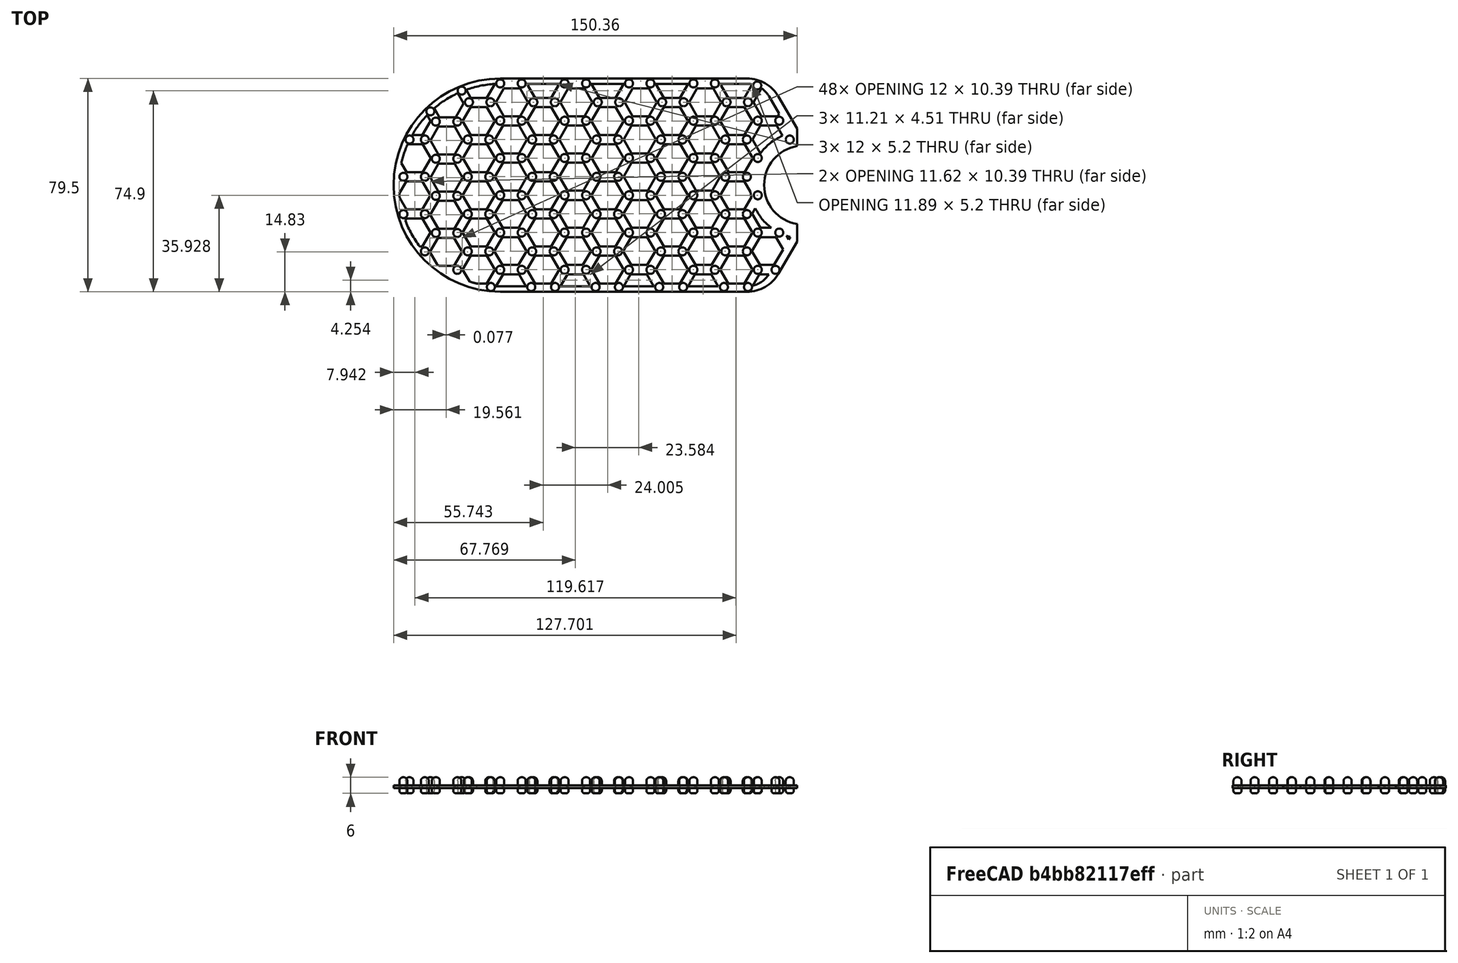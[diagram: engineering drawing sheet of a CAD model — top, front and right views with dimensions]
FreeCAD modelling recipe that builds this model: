
FCSTD DOCUMENT  (FreeCAD 1.0R39319 (Git))
Label: Soap_dryer
License: All rights reserved
LicenseURL: https://en.wikipedia.org/wiki/All_rights_reserved
objects: Sketcher::SketchObject×2, PartDesign::Pad×2, PartDesign::Fillet×2, PartDesign::Body×1
note: 17 computed .brp shape members not serialized (recipe doc carries the construction recipe); baked Part::Feature solids carry a one-line shape summary decoded from their .brp

FEATURE [Sketcher::SketchObject] Sketch
  ArcFitTolerance = 1e-06
  FullyConstrained = true
  MakeInternals = false
  sketch-geometry (463):
    g0: GeomPoint [constr] X=-7.3e-15 Y=0 Z=0
    g1: ArcOfCircle CenterX=-7.3e-15 CenterY=0 CenterZ=0 NormalX=0 NormalY=0 NormalZ=1 AngleXU=0 Radius=39.75 StartAngle=1.5708 EndAngle=4.71239
    g2: GeomPoint [constr] X=113.11 Y=0 Z=0
    g3: GeomPoint [constr] X=110.61 Y=14.5366 Z=0
    g4: GeomPoint [constr] X=110.61 Y=-14.5366 Z=0
    g5: ArcOfCircle CenterX=113.11 CenterY=0 CenterZ=0 NormalX=0 NormalY=0 NormalZ=1 AngleXU=0 Radius=14.75 StartAngle=1.74111 EndAngle=4.54208
    g6: LineSegment StartX=-7.3e-15 StartY=39.75 StartZ=0 EndX=92 EndY=39.75 EndZ=0
    g7: LineSegment StartX=-7.3e-15 StartY=-39.75 StartZ=0 EndX=92 EndY=-39.75 EndZ=0
    g8: GeomPoint [constr] X=98.11 Y=39.75 Z=0
    g9: ArcOfCircle CenterX=92 CenterY=-26.25 CenterZ=0 NormalX=0 NormalY=0 NormalZ=1 AngleXU=0 Radius=13.5 StartAngle=4.71239 EndAngle=5.75886
    g10: GeomPoint [constr] X=98.11 Y=-39.75 Z=0
    g11: ArcOfCircle [constr] CenterX=-7.3e-15 CenterY=0 CenterZ=0 NormalX=0 NormalY=0 NormalZ=1 AngleXU=0 Radius=37.75 StartAngle=1.5708 EndAngle=4.71239
    g12: LineSegment [constr] StartX=0 StartY=37.75 StartZ=0 EndX=92 EndY=37.75 EndZ=0
    g13: LineSegment [constr] StartX=100.219 StartY=33.0085 StartZ=0 EndX=108.11 EndY=19.3649 EndZ=0
    g14: ArcOfCircle [constr] CenterX=113.11 CenterY=0 CenterZ=0 NormalX=0 NormalY=0 NormalZ=1 AngleXU=0 Radius=20 StartAngle=1.82349 EndAngle=4.4597
    g15: ArcOfCircle [constr] CenterX=92 CenterY=28.255 CenterZ=0 NormalX=0 NormalY=0 NormalZ=1 AngleXU=0 Radius=9.49497 StartAngle=0.524324 EndAngle=1.5708
    g16: GeomPoint [constr] X=97.4773 Y=37.75 Z=0
    g17: LineSegment [constr] StartX=0 StartY=-37.75 StartZ=0 EndX=92 EndY=-37.75 EndZ=0
    g18: LineSegment [constr] StartX=100.219 StartY=-33.0085 StartZ=0 EndX=108.11 EndY=-19.3649 EndZ=0
    g19: ArcOfCircle [constr] CenterX=92 CenterY=-28.255 CenterZ=0 NormalX=0 NormalY=0 NormalZ=1 AngleXU=0 Radius=9.49497 StartAngle=4.71239 EndAngle=5.75886
    g20: GeomPoint [constr] X=97.4773 Y=-37.75 Z=0
    g21: LineSegment [constr] StartX=92 StartY=-39.75 StartZ=0 EndX=92 EndY=-37.75 EndZ=0
    g22: LineSegment StartX=110.61 StartY=14.5366 StartZ=0 EndX=110.61 EndY=21.0366 EndZ=0
    g23: LineSegment StartX=110.61 StartY=21.0366 StartZ=0 EndX=103.686 EndY=33.0085 EndZ=0
    g24: ArcOfCircle CenterX=92 CenterY=26.25 CenterZ=0 NormalX=0 NormalY=0 NormalZ=1 AngleXU=0 Radius=13.5 StartAngle=0.524324 EndAngle=1.5708
    g25: LineSegment StartX=110.61 StartY=-14.5366 StartZ=0 EndX=110.61 EndY=-21.0366 EndZ=0
    g26: LineSegment StartX=103.686 StartY=-33.0085 StartZ=0 EndX=110.61 EndY=-21.0366 EndZ=0
    g27: LineSegment StartX=10.3593 StartY=30.8238 StartZ=0 EndX=7.35933 EndY=36.02 EndZ=0
    g28: LineSegment StartX=7.35933 StartY=36.02 StartZ=0 EndX=1.35933 EndY=36.02 EndZ=0
    g29: LineSegment StartX=1.35933 StartY=36.02 StartZ=0 EndX=-1.64067 EndY=30.8238 EndZ=0
    g30: LineSegment StartX=-1.64067 StartY=30.8238 StartZ=0 EndX=1.35933 EndY=25.6277 EndZ=0
    g31: LineSegment StartX=1.35933 StartY=25.6277 StartZ=0 EndX=7.35933 EndY=25.6277 EndZ=0
    g32: LineSegment StartX=7.35933 StartY=25.6277 StartZ=0 EndX=10.3593 EndY=30.8238 EndZ=0
    g33: Circle [constr] CenterX=4.35933 CenterY=30.8238 CenterZ=0 NormalX=0 NormalY=0 NormalZ=1 AngleXU=0 Radius=6
    g34: LineSegment StartX=12.9933 StartY=32.55 StartZ=0 EndX=18.9933 EndY=32.55 EndZ=0
    g35: LineSegment StartX=12.9933 StartY=32.55 StartZ=0 EndX=9.99111 EndY=37.75 EndZ=0
    g36: LineSegment StartX=18.9933 StartY=32.55 StartZ=0 EndX=21.9956 EndY=37.75 EndZ=0
    g37: LineSegment StartX=36.9978 StartY=32.55 StartZ=0 EndX=42.9978 EndY=32.55 EndZ=0
    g38: LineSegment StartX=36.9978 StartY=32.55 StartZ=0 EndX=33.9956 EndY=37.75 EndZ=0
    g39: LineSegment StartX=42.9978 StartY=32.55 StartZ=0 EndX=46 EndY=37.75 EndZ=0
    g40: LineSegment StartX=61.0022 StartY=32.55 StartZ=0 EndX=67.0022 EndY=32.55 EndZ=0
    g41: LineSegment StartX=61.0022 StartY=32.55 StartZ=0 EndX=58 EndY=37.75 EndZ=0
    g42: LineSegment StartX=67.0022 StartY=32.55 StartZ=0 EndX=70.0044 EndY=37.75 EndZ=0
    g43: LineSegment StartX=85.0067 StartY=32.55 StartZ=0 EndX=91.0067 EndY=32.55 EndZ=0
    g44: LineSegment StartX=85.0067 StartY=32.55 StartZ=0 EndX=82.0044 EndY=37.75 EndZ=0
    g45: LineSegment StartX=91.0067 StartY=32.55 StartZ=0 EndX=93.8982 EndY=37.5583 EndZ=0
    g46: LineSegment StartX=94.3593 StartY=30.8967 StartZ=0 EndX=97.3593 EndY=25.7006 EndZ=0
    g47: LineSegment StartX=97.3593 StartY=25.7006 StartZ=0 EndX=103.359 EndY=25.7006 EndZ=0
    g48: LineSegment StartX=94.3593 StartY=30.8967 StartZ=0 EndX=97.3593 EndY=36.0929 EndZ=0
    g49: LineSegment StartX=103.359 StartY=25.7006 StartZ=0 EndX=103.902 EndY=26.6406 EndZ=0
    g50: LineSegment StartX=-22.6407 StartY=25.293 StartZ=0 EndX=-16.6407 EndY=25.293 EndZ=0
    g51: LineSegment StartX=-16.6407 StartY=25.293 StartZ=0 EndX=-13.6407 EndY=30.4891 EndZ=0
    g52: LineSegment StartX=-13.6407 StartY=30.4891 StartZ=0 EndX=-15.8252 EndY=34.2728 EndZ=0
    g53: LineSegment StartX=-26 StartY=23.883 StartZ=0 EndX=-29 EndY=18.6868 EndZ=0
    g54: LineSegment StartX=-29 StartY=18.6868 StartZ=0 EndX=-32.8004 EndY=18.6868 EndZ=0
    g55: LineSegment StartX=-26 StartY=23.883 StartZ=0 EndX=-27.2776 EndY=26.0959 EndZ=0
    g56: LineSegment StartX=-34.9123 StartY=4.83453 StartZ=0 EndX=-28.9123 EndY=4.83453 EndZ=0
    g57: LineSegment StartX=-28.9123 StartY=4.83453 StartZ=0 EndX=-25.9123 EndY=10.0307 EndZ=0
    g58: LineSegment StartX=-25.9123 StartY=10.0307 StartZ=0 EndX=-28.9123 EndY=15.2268 EndZ=0
    g59: LineSegment StartX=-28.9123 StartY=15.2268 StartZ=0 EndX=-34.5428 EndY=15.2268 EndZ=0
    g60: LineSegment StartX=-34.9123 StartY=4.83453 StartZ=0 EndX=-36.8505 EndY=8.19164 EndZ=0
    g61: LineSegment StartX=-34.9978 StartY=1.37453 StartZ=0 EndX=-28.9978 EndY=1.37453 EndZ=0
    g62: LineSegment StartX=-28.9978 StartY=1.37453 StartZ=0 EndX=-25.9978 EndY=-3.82162 EndZ=0
    g63: LineSegment StartX=-25.9978 StartY=-3.82162 StartZ=0 EndX=-28.9978 EndY=-9.01778 EndZ=0
    g64: LineSegment StartX=-28.9978 StartY=-9.01778 StartZ=0 EndX=-34.9978 EndY=-9.01778 EndZ=0
    g65: LineSegment StartX=-34.9978 StartY=-9.01778 StartZ=0 EndX=-37.4466 EndY=-4.77619 EndZ=0
    g66: LineSegment StartX=-34.9978 StartY=1.37453 StartZ=0 EndX=-37.6173 EndY=-3.16263 EndZ=0
    g67: LineSegment StartX=-35.0184 StartY=-12.4778 StartZ=0 EndX=-29.0184 EndY=-12.4778 EndZ=0
    g68: LineSegment StartX=-29.0184 StartY=-12.4778 StartZ=0 EndX=-26.0184 EndY=-17.6739 EndZ=0
    g69: LineSegment StartX=-26.0184 StartY=-17.6739 StartZ=0 EndX=-29.0184 EndY=-22.8701 EndZ=0
    g70: LineSegment StartX=-29.0184 StartY=-22.8701 StartZ=0 EndX=-30.0337 EndY=-22.8701 EndZ=0
    g71: LineSegment StartX=-35.0184 StartY=-12.4778 StartZ=0 EndX=-35.3938 EndY=-13.1279 EndZ=0
    g72: LineSegment StartX=-23.1895 StartY=-19.7239 StartZ=0 EndX=-17.1895 EndY=-19.7239 EndZ=0
    g73: LineSegment StartX=-17.1895 StartY=-19.7239 StartZ=0 EndX=-14.1895 EndY=-24.9201 EndZ=0
    g74: LineSegment StartX=-14.1895 StartY=-24.9201 StartZ=0 EndX=-17.1895 EndY=-30.1162 EndZ=0
    g75: LineSegment StartX=-23.1895 StartY=-19.7239 StartZ=0 EndX=-26.1895 EndY=-24.9201 EndZ=0
    g76: LineSegment StartX=-11 StartY=-26.3338 StartZ=0 EndX=-5.00001 EndY=-26.3338 EndZ=0
    g77: LineSegment StartX=-11 StartY=-26.3338 StartZ=0 EndX=-14 EndY=-31.5299 EndZ=0
    g78: LineSegment StartX=-14 StartY=-31.5299 StartZ=0 EndX=-11.4323 EndY=-35.9773 EndZ=0
    g79: LineSegment StartX=-5.00001 StartY=-26.3338 StartZ=0 EndX=-2.00001 EndY=-31.5299 EndZ=0
    g80: LineSegment StartX=-2.00001 StartY=-31.5299 StartZ=0 EndX=-5.00001 EndY=-36.7261 EndZ=0
    g81: LineSegment StartX=-5.00001 StartY=-36.7261 StartZ=0 EndX=-8.73249 EndY=-36.7261 EndZ=0
    g82: LineSegment StartX=57.9973 StartY=16.9715 StartZ=0 EndX=54.9973 EndY=22.1677 EndZ=0
    g83: LineSegment StartX=54.9973 StartY=22.1677 StartZ=0 EndX=48.9973 EndY=22.1677 EndZ=0
    g84: LineSegment StartX=48.9973 StartY=22.1677 StartZ=0 EndX=45.9973 EndY=16.9715 EndZ=0
    g85: LineSegment StartX=45.9973 StartY=16.9715 StartZ=0 EndX=48.9973 EndY=11.7754 EndZ=0
    g86: LineSegment StartX=48.9973 StartY=11.7754 StartZ=0 EndX=54.9973 EndY=11.7754 EndZ=0
    g87: LineSegment StartX=54.9973 StartY=11.7754 StartZ=0 EndX=57.9973 EndY=16.9715 EndZ=0
    g88: Circle [constr] CenterX=51.9973 CenterY=16.9715 CenterZ=0 NormalX=0 NormalY=0 NormalZ=1 AngleXU=0 Radius=6
    g89: LineSegment StartX=46 StartY=23.8938 StartZ=0 EndX=43 EndY=29.09 EndZ=0
    g90: LineSegment StartX=43 StartY=29.09 StartZ=0 EndX=37 EndY=29.09 EndZ=0
    g91: LineSegment StartX=37 StartY=29.09 StartZ=0 EndX=34 EndY=23.8938 EndZ=0
    g92: LineSegment StartX=34 StartY=23.8938 StartZ=0 EndX=37 EndY=18.6977 EndZ=0
    g93: LineSegment StartX=37 StartY=18.6977 StartZ=0 EndX=43 EndY=18.6977 EndZ=0
    g94: LineSegment StartX=43 StartY=18.6977 StartZ=0 EndX=46 EndY=23.8938 EndZ=0
    g95: Circle [constr] CenterX=40 CenterY=23.8938 CenterZ=0 NormalX=0 NormalY=0 NormalZ=1 AngleXU=0 Radius=6
    g96: LineSegment StartX=70 StartY=23.8938 StartZ=0 EndX=67 EndY=29.09 EndZ=0
    g97: LineSegment StartX=67 StartY=29.09 StartZ=0 EndX=61 EndY=29.09 EndZ=0
    g98: LineSegment StartX=61 StartY=29.09 StartZ=0 EndX=58 EndY=23.8938 EndZ=0
    g99: LineSegment StartX=58 StartY=23.8938 StartZ=0 EndX=61 EndY=18.6977 EndZ=0
    g100: LineSegment StartX=61 StartY=18.6977 StartZ=0 EndX=67 EndY=18.6977 EndZ=0
    g101: LineSegment StartX=67 StartY=18.6977 StartZ=0 EndX=70 EndY=23.8938 EndZ=0
    g102: Circle [constr] CenterX=64 CenterY=23.8938 CenterZ=0 NormalX=0 NormalY=0 NormalZ=1 AngleXU=0 Radius=6
    g103: LineSegment StartX=82.3593 StartY=30.8238 StartZ=0 EndX=79.3593 EndY=36.02 EndZ=0
    g104: LineSegment StartX=79.3593 StartY=36.02 StartZ=0 EndX=73.3593 EndY=36.02 EndZ=0
    g105: LineSegment StartX=73.3593 StartY=36.02 StartZ=0 EndX=70.3593 EndY=30.8238 EndZ=0
    g106: LineSegment StartX=70.3593 StartY=30.8238 StartZ=0 EndX=73.3593 EndY=25.6277 EndZ=0
    g107: LineSegment StartX=73.3593 StartY=25.6277 StartZ=0 EndX=79.3593 EndY=25.6277 EndZ=0
    g108: LineSegment StartX=79.3593 StartY=25.6277 StartZ=0 EndX=82.3593 EndY=30.8238 EndZ=0
    g109: Circle [constr] CenterX=76.3593 CenterY=30.8238 CenterZ=0 NormalX=0 NormalY=0 NormalZ=1 AngleXU=0 Radius=6
    g110: LineSegment StartX=94 StartY=23.8938 StartZ=0 EndX=91 EndY=29.09 EndZ=0
    g111: LineSegment StartX=91 StartY=29.09 StartZ=0 EndX=85 EndY=29.09 EndZ=0
    g112: LineSegment StartX=85 StartY=29.09 StartZ=0 EndX=82 EndY=23.8938 EndZ=0
    g113: LineSegment StartX=82 StartY=23.8938 StartZ=0 EndX=85 EndY=18.6977 EndZ=0
    g114: LineSegment StartX=85 StartY=18.6977 StartZ=0 EndX=91 EndY=18.6977 EndZ=0
    g115: LineSegment StartX=91 StartY=18.6977 StartZ=0 EndX=94 EndY=23.8938 EndZ=0
    g116: Circle [constr] CenterX=88 CenterY=23.8938 CenterZ=0 NormalX=0 NormalY=0 NormalZ=1 AngleXU=0 Radius=6
    g117: LineSegment StartX=58.3593 StartY=30.8238 StartZ=0 EndX=55.3593 EndY=36.02 EndZ=0
    g118: LineSegment StartX=55.3593 StartY=36.02 StartZ=0 EndX=49.3593 EndY=36.02 EndZ=0
    g119: LineSegment StartX=49.3593 StartY=36.02 StartZ=0 EndX=46.3593 EndY=30.8238 EndZ=0
    g120: LineSegment StartX=46.3593 StartY=30.8238 StartZ=0 EndX=49.3593 EndY=25.6277 EndZ=0
    g121: LineSegment StartX=49.3593 StartY=25.6277 StartZ=0 EndX=55.3593 EndY=25.6277 EndZ=0
    g122: LineSegment StartX=55.3593 StartY=25.6277 StartZ=0 EndX=58.3593 EndY=30.8238 EndZ=0
    g123: Circle [constr] CenterX=52.3593 CenterY=30.8238 CenterZ=0 NormalX=0 NormalY=0 NormalZ=1 AngleXU=0 Radius=6
    g124: LineSegment StartX=34.3593 StartY=30.8238 StartZ=0 EndX=31.3593 EndY=36.02 EndZ=0
    g125: LineSegment StartX=31.3593 StartY=36.02 StartZ=0 EndX=25.3593 EndY=36.02 EndZ=0
    g126: LineSegment StartX=25.3593 StartY=36.02 StartZ=0 EndX=22.3593 EndY=30.8238 EndZ=0
    g127: LineSegment StartX=22.3593 StartY=30.8238 StartZ=0 EndX=25.3593 EndY=25.6277 EndZ=0
    g128: LineSegment StartX=25.3593 StartY=25.6277 StartZ=0 EndX=31.3593 EndY=25.6277 EndZ=0
    g129: LineSegment StartX=31.3593 StartY=25.6277 StartZ=0 EndX=34.3593 EndY=30.8238 EndZ=0
    g130: Circle [constr] CenterX=28.3593 CenterY=30.8238 CenterZ=0 NormalX=0 NormalY=0 NormalZ=1 AngleXU=0 Radius=6
    g131: LineSegment StartX=22 StartY=23.8938 StartZ=0 EndX=19 EndY=29.09 EndZ=0
    g132: LineSegment StartX=19 StartY=29.09 StartZ=0 EndX=13 EndY=29.09 EndZ=0
    g133: LineSegment StartX=13 StartY=29.09 StartZ=0 EndX=10 EndY=23.8938 EndZ=0
    g134: LineSegment StartX=10 StartY=23.8938 StartZ=0 EndX=13 EndY=18.6977 EndZ=0
    g135: LineSegment StartX=13 StartY=18.6977 StartZ=0 EndX=19 EndY=18.6977 EndZ=0
    g136: LineSegment StartX=19 StartY=18.6977 StartZ=0 EndX=22 EndY=23.8938 EndZ=0
    g137: Circle [constr] CenterX=16 CenterY=23.8938 CenterZ=0 NormalX=0 NormalY=0 NormalZ=1 AngleXU=0 Radius=6
    g138: LineSegment StartX=9.99732 StartY=16.9715 StartZ=0 EndX=6.99732 EndY=22.1677 EndZ=0
    g139: LineSegment StartX=6.99732 StartY=22.1677 StartZ=0 EndX=0.997325 EndY=22.1677 EndZ=0
    g140: LineSegment StartX=0.997325 StartY=22.1677 StartZ=0 EndX=-2.00268 EndY=16.9715 EndZ=0
    g141: LineSegment StartX=-2.00268 StartY=16.9715 StartZ=0 EndX=0.997325 EndY=11.7754 EndZ=0
    g142: LineSegment StartX=0.997325 StartY=11.7754 StartZ=0 EndX=6.99732 EndY=11.7754 EndZ=0
    g143: LineSegment StartX=6.99732 StartY=11.7754 StartZ=0 EndX=9.99732 EndY=16.9715 EndZ=0
    g144: Circle [constr] CenterX=3.99732 CenterY=16.9715 CenterZ=0 NormalX=0 NormalY=0 NormalZ=1 AngleXU=0 Radius=6
    g145: LineSegment StartX=-2 StartY=23.8793 StartZ=0 EndX=-5 EndY=29.0754 EndZ=0
    g146: LineSegment StartX=-5 StartY=29.0754 StartZ=0 EndX=-11 EndY=29.0754 EndZ=0
    g147: LineSegment StartX=-11 StartY=29.0754 StartZ=0 EndX=-14 EndY=23.8793 EndZ=0
    g148: LineSegment StartX=-14 StartY=23.8793 StartZ=0 EndX=-11 EndY=18.6831 EndZ=0
    g149: LineSegment StartX=-11 StartY=18.6831 StartZ=0 EndX=-5 EndY=18.6831 EndZ=0
    g150: LineSegment StartX=-5 StartY=18.6831 StartZ=0 EndX=-2 EndY=23.8793 EndZ=0
    g151: Circle [constr] CenterX=-8 CenterY=23.8793 CenterZ=0 NormalX=0 NormalY=0 NormalZ=1 AngleXU=0 Radius=6
    g152: LineSegment StartX=-14.0027 StartY=16.6368 StartZ=0 EndX=-17.0027 EndY=21.833 EndZ=0
    g153: LineSegment StartX=-17.0027 StartY=21.833 StartZ=0 EndX=-23.0027 EndY=21.833 EndZ=0
    g154: LineSegment StartX=-23.0027 StartY=21.833 StartZ=0 EndX=-26.0027 EndY=16.6368 EndZ=0
    g155: LineSegment StartX=-26.0027 StartY=16.6368 StartZ=0 EndX=-23.0027 EndY=11.4407 EndZ=0
    g156: LineSegment StartX=-23.0027 StartY=11.4407 StartZ=0 EndX=-17.0027 EndY=11.4407 EndZ=0
    g157: LineSegment StartX=-17.0027 StartY=11.4407 StartZ=0 EndX=-14.0027 EndY=16.6368 EndZ=0
    g158: Circle [constr] CenterX=-20.0027 CenterY=16.6368 CenterZ=0 NormalX=0 NormalY=0 NormalZ=1 AngleXU=0 Radius=6
    g159: LineSegment StartX=-1.91227 StartY=10.027 StartZ=0 EndX=-4.91227 EndY=15.2231 EndZ=0
    g160: LineSegment StartX=-4.91227 StartY=15.2231 StartZ=0 EndX=-10.9123 EndY=15.2231 EndZ=0
    g161: LineSegment StartX=-10.9123 StartY=15.2231 StartZ=0 EndX=-13.9123 EndY=10.027 EndZ=0
    g162: LineSegment StartX=-13.9123 StartY=10.027 StartZ=0 EndX=-10.9123 EndY=4.83082 EndZ=0
    g163: LineSegment StartX=-10.9123 StartY=4.83082 StartZ=0 EndX=-4.91227 EndY=4.83082 EndZ=0
    g164: LineSegment StartX=-4.91227 StartY=4.83082 StartZ=0 EndX=-1.91227 EndY=10.027 EndZ=0
    g165: Circle [constr] CenterX=-7.91227 CenterY=10.027 CenterZ=0 NormalX=0 NormalY=0 NormalZ=1 AngleXU=0 Radius=6
    g166: LineSegment StartX=-14 StartY=2.78453 StartZ=0 EndX=-17 EndY=7.98068 EndZ=0
    g167: LineSegment StartX=-17 StartY=7.98068 StartZ=0 EndX=-23 EndY=7.98068 EndZ=0
    g168: LineSegment StartX=-23 StartY=7.98068 StartZ=0 EndX=-26 EndY=2.78453 EndZ=0
    g169: LineSegment StartX=-26 StartY=2.78453 StartZ=0 EndX=-23 EndY=-2.41162 EndZ=0
    g170: LineSegment StartX=-23 StartY=-2.41162 StartZ=0 EndX=-17 EndY=-2.41162 EndZ=0
    g171: LineSegment StartX=-17 StartY=-2.41162 StartZ=0 EndX=-14 EndY=2.78453 EndZ=0
    g172: Circle [constr] CenterX=-20 CenterY=2.78453 CenterZ=0 NormalX=0 NormalY=0 NormalZ=1 AngleXU=0 Radius=6
    g173: LineSegment StartX=-14.1129 StartY=-11.0678 StartZ=0 EndX=-17.1129 EndY=-5.87162 EndZ=0
    g174: LineSegment StartX=-17.1129 StartY=-5.87162 StartZ=0 EndX=-23.1129 EndY=-5.87162 EndZ=0
    g175: LineSegment StartX=-23.1129 StartY=-5.87162 StartZ=0 EndX=-26.1129 EndY=-11.0678 EndZ=0
    g176: LineSegment StartX=-26.1129 StartY=-11.0678 StartZ=0 EndX=-23.1129 EndY=-16.2639 EndZ=0
    g177: LineSegment StartX=-23.1129 StartY=-16.2639 StartZ=0 EndX=-17.1129 EndY=-16.2639 EndZ=0
    g178: LineSegment StartX=-17.1129 StartY=-16.2639 StartZ=0 EndX=-14.1129 EndY=-11.0678 EndZ=0
    g179: Circle [constr] CenterX=-20.1129 CenterY=-11.0678 CenterZ=0 NormalX=0 NormalY=0 NormalZ=1 AngleXU=0 Radius=6
    g180: LineSegment StartX=-1.99776 StartY=-3.82533 StartZ=0 EndX=-4.99776 EndY=1.37082 EndZ=0
    g181: LineSegment StartX=-4.99776 StartY=1.37082 StartZ=0 EndX=-10.9978 EndY=1.37082 EndZ=0
    g182: LineSegment StartX=-10.9978 StartY=1.37082 StartZ=0 EndX=-13.9978 EndY=-3.82533 EndZ=0
    g183: LineSegment StartX=-13.9978 StartY=-3.82533 StartZ=0 EndX=-10.9978 EndY=-9.02149 EndZ=0
    g184: LineSegment StartX=-10.9978 StartY=-9.02149 StartZ=0 EndX=-4.99776 EndY=-9.02149 EndZ=0
    g185: LineSegment StartX=-4.99776 StartY=-9.02149 StartZ=0 EndX=-1.99776 EndY=-3.82533 EndZ=0
    g186: Circle [constr] CenterX=-7.99776 CenterY=-3.82533 CenterZ=0 NormalX=0 NormalY=0 NormalZ=1 AngleXU=0 Radius=6
    g187: LineSegment StartX=-2.0184 StartY=-17.6776 StartZ=0 EndX=-5.0184 EndY=-12.4815 EndZ=0
    g188: LineSegment StartX=-5.0184 StartY=-12.4815 StartZ=0 EndX=-11.0184 EndY=-12.4815 EndZ=0
    g189: LineSegment StartX=-11.0184 StartY=-12.4815 StartZ=0 EndX=-14.0184 EndY=-17.6776 EndZ=0
    g190: LineSegment StartX=-14.0184 StartY=-17.6776 StartZ=0 EndX=-11.0184 EndY=-22.8738 EndZ=0
    g191: LineSegment StartX=-11.0184 StartY=-22.8738 StartZ=0 EndX=-5.0184 EndY=-22.8738 EndZ=0
    g192: LineSegment StartX=-5.0184 StartY=-22.8738 StartZ=0 EndX=-2.0184 EndY=-17.6776 EndZ=0
    g193: Circle [constr] CenterX=-8.0184 CenterY=-17.6776 CenterZ=0 NormalX=0 NormalY=0 NormalZ=1 AngleXU=0 Radius=6
    g194: LineSegment StartX=9.81053 StartY=-24.5854 StartZ=0 EndX=6.81053 EndY=-19.3892 EndZ=0
    g195: LineSegment StartX=6.81053 StartY=-19.3892 StartZ=0 EndX=0.81053 EndY=-19.3892 EndZ=0
    g196: LineSegment StartX=0.81053 StartY=-19.3892 StartZ=0 EndX=-2.18947 EndY=-24.5854 EndZ=0
    g197: LineSegment StartX=-2.18947 StartY=-24.5854 StartZ=0 EndX=0.81053 EndY=-29.7815 EndZ=0
    g198: LineSegment StartX=0.81053 StartY=-29.7815 StartZ=0 EndX=6.81053 EndY=-29.7815 EndZ=0
    g199: LineSegment StartX=6.81053 StartY=-29.7815 StartZ=0 EndX=9.81053 EndY=-24.5854 EndZ=0
    g200: Circle [constr] CenterX=3.81053 CenterY=-24.5854 CenterZ=0 NormalX=0 NormalY=0 NormalZ=1 AngleXU=0 Radius=6
    g201: LineSegment StartX=7.01885 StartY=-33.2415 StartZ=0 EndX=1.01885 EndY=-33.2415 EndZ=0
    g202: LineSegment StartX=1.01885 StartY=-33.2415 StartZ=0 EndX=-1.56537 EndY=-37.7175 EndZ=0
    g203: LineSegment StartX=7.01885 StartY=-33.2415 StartZ=0 EndX=9.62182 EndY=-37.75 EndZ=0
    g204: LineSegment StartX=10 StartY=3.11924 StartZ=0 EndX=7 EndY=8.31539 EndZ=0
    g205: LineSegment StartX=7 StartY=8.31539 StartZ=0 EndX=1 EndY=8.31539 EndZ=0
    g206: LineSegment StartX=1 StartY=8.31539 StartZ=0 EndX=-2 EndY=3.11924 EndZ=0
    g207: LineSegment StartX=-2 StartY=3.11924 StartZ=0 EndX=1 EndY=-2.07691 EndZ=0
    g208: LineSegment StartX=1 StartY=-2.07691 StartZ=0 EndX=7 EndY=-2.07691 EndZ=0
    g209: LineSegment StartX=7 StartY=-2.07691 StartZ=0 EndX=10 EndY=3.11924 EndZ=0
    g210: Circle [constr] CenterX=4 CenterY=3.11924 CenterZ=0 NormalX=0 NormalY=0 NormalZ=1 AngleXU=0 Radius=6
    g211: LineSegment StartX=22.0877 StartY=10.0415 StartZ=0 EndX=19.0877 EndY=15.2377 EndZ=0
    g212: LineSegment StartX=19.0877 StartY=15.2377 StartZ=0 EndX=13.0877 EndY=15.2377 EndZ=0
    g213: LineSegment StartX=13.0877 StartY=15.2377 StartZ=0 EndX=10.0877 EndY=10.0415 EndZ=0
    g214: LineSegment StartX=10.0877 StartY=10.0415 StartZ=0 EndX=13.0877 EndY=4.84539 EndZ=0
    g215: LineSegment StartX=13.0877 StartY=4.84539 StartZ=0 EndX=19.0877 EndY=4.84539 EndZ=0
    g216: LineSegment StartX=19.0877 StartY=4.84539 StartZ=0 EndX=22.0877 EndY=10.0415 EndZ=0
    g217: Circle [constr] CenterX=16.0877 CenterY=10.0415 CenterZ=0 NormalX=0 NormalY=0 NormalZ=1 AngleXU=0 Radius=6
    g218: LineSegment StartX=33.9973 StartY=16.9715 StartZ=0 EndX=30.9973 EndY=22.1677 EndZ=0
    g219: LineSegment StartX=30.9973 StartY=22.1677 StartZ=0 EndX=24.9973 EndY=22.1677 EndZ=0
    g220: LineSegment StartX=24.9973 StartY=22.1677 StartZ=0 EndX=21.9973 EndY=16.9715 EndZ=0
    g221: LineSegment StartX=21.9973 StartY=16.9715 StartZ=0 EndX=24.9973 EndY=11.7754 EndZ=0
    g222: LineSegment StartX=24.9973 StartY=11.7754 StartZ=0 EndX=30.9973 EndY=11.7754 EndZ=0
    g223: LineSegment StartX=30.9973 StartY=11.7754 StartZ=0 EndX=33.9973 EndY=16.9715 EndZ=0
    g224: Circle [constr] CenterX=27.9973 CenterY=16.9715 CenterZ=0 NormalX=0 NormalY=0 NormalZ=1 AngleXU=0 Radius=6
    g225: LineSegment StartX=9.88715 StartY=-10.7331 StartZ=0 EndX=6.88715 EndY=-5.53691 EndZ=0
    g226: LineSegment StartX=6.88715 StartY=-5.53691 StartZ=0 EndX=0.887149 EndY=-5.53691 EndZ=0
    g227: LineSegment StartX=0.887149 StartY=-5.53691 StartZ=0 EndX=-2.11285 EndY=-10.7331 EndZ=0
    g228: LineSegment StartX=-2.11285 StartY=-10.7331 StartZ=0 EndX=0.887149 EndY=-15.9292 EndZ=0
    g229: LineSegment StartX=0.887149 StartY=-15.9292 StartZ=0 EndX=6.88715 EndY=-15.9292 EndZ=0
    g230: LineSegment StartX=6.88715 StartY=-15.9292 StartZ=0 EndX=9.88715 EndY=-10.7331 EndZ=0
    g231: Circle [constr] CenterX=3.88715 CenterY=-10.7331 CenterZ=0 NormalX=0 NormalY=0 NormalZ=1 AngleXU=0 Radius=6
    g232: LineSegment StartX=22.0022 StartY=-3.81076 StartZ=0 EndX=19.0022 EndY=1.38539 EndZ=0
    g233: LineSegment StartX=19.0022 StartY=1.38539 StartZ=0 EndX=13.0022 EndY=1.38539 EndZ=0
    g234: LineSegment StartX=13.0022 StartY=1.38539 StartZ=0 EndX=10.0022 EndY=-3.81076 EndZ=0
    g235: LineSegment StartX=10.0022 StartY=-3.81076 StartZ=0 EndX=13.0022 EndY=-9.00691 EndZ=0
    g236: LineSegment StartX=13.0022 StartY=-9.00691 StartZ=0 EndX=19.0022 EndY=-9.00691 EndZ=0
    g237: LineSegment StartX=19.0022 StartY=-9.00691 StartZ=0 EndX=22.0022 EndY=-3.81076 EndZ=0
    g238: Circle [constr] CenterX=16.0022 CenterY=-3.81076 CenterZ=0 NormalX=0 NormalY=0 NormalZ=1 AngleXU=0 Radius=6
    g239: LineSegment StartX=21.9816 StartY=-17.6631 StartZ=0 EndX=18.9816 EndY=-12.4669 EndZ=0
    g240: LineSegment StartX=18.9816 StartY=-12.4669 StartZ=0 EndX=12.9816 EndY=-12.4669 EndZ=0
    g241: LineSegment StartX=12.9816 StartY=-12.4669 StartZ=0 EndX=9.9816 EndY=-17.6631 EndZ=0
    g242: LineSegment StartX=9.9816 StartY=-17.6631 StartZ=0 EndX=12.9816 EndY=-22.8592 EndZ=0
    g243: LineSegment StartX=12.9816 StartY=-22.8592 StartZ=0 EndX=18.9816 EndY=-22.8592 EndZ=0
    g244: LineSegment StartX=18.9816 StartY=-22.8592 StartZ=0 EndX=21.9816 EndY=-17.6631 EndZ=0
    g245: Circle [constr] CenterX=15.9816 CenterY=-17.6631 CenterZ=0 NormalX=0 NormalY=0 NormalZ=1 AngleXU=0 Radius=6
    g246: LineSegment StartX=46.0877 StartY=10.0415 StartZ=0 EndX=43.0877 EndY=15.2377 EndZ=0
    g247: LineSegment StartX=43.0877 StartY=15.2377 StartZ=0 EndX=37.0877 EndY=15.2377 EndZ=0
    g248: LineSegment StartX=37.0877 StartY=15.2377 StartZ=0 EndX=34.0877 EndY=10.0415 EndZ=0
    g249: LineSegment StartX=34.0877 StartY=10.0415 StartZ=0 EndX=37.0877 EndY=4.84539 EndZ=0
    g250: LineSegment StartX=37.0877 StartY=4.84539 StartZ=0 EndX=43.0877 EndY=4.84539 EndZ=0
    g251: LineSegment StartX=43.0877 StartY=4.84539 StartZ=0 EndX=46.0877 EndY=10.0415 EndZ=0
    g252: Circle [constr] CenterX=40.0877 CenterY=10.0415 CenterZ=0 NormalX=0 NormalY=0 NormalZ=1 AngleXU=0 Radius=6
    g253: LineSegment StartX=34 StartY=3.11924 StartZ=0 EndX=31 EndY=8.31539 EndZ=0
    g254: LineSegment StartX=31 StartY=8.31539 StartZ=0 EndX=25 EndY=8.31539 EndZ=0
    g255: LineSegment StartX=25 StartY=8.31539 StartZ=0 EndX=22 EndY=3.11924 EndZ=0
    g256: LineSegment StartX=22 StartY=3.11924 StartZ=0 EndX=25 EndY=-2.07691 EndZ=0
    g257: LineSegment StartX=25 StartY=-2.07691 StartZ=0 EndX=31 EndY=-2.07691 EndZ=0
    g258: LineSegment StartX=31 StartY=-2.07691 StartZ=0 EndX=34 EndY=3.11924 EndZ=0
    g259: Circle [constr] CenterX=28 CenterY=3.11924 CenterZ=0 NormalX=0 NormalY=0 NormalZ=1 AngleXU=0 Radius=6
    g260: LineSegment StartX=70.0044 StartY=37.75 StartZ=0 EndX=58 EndY=37.75 EndZ=0
    g261: LineSegment StartX=46 StartY=37.75 StartZ=0 EndX=33.9956 EndY=37.75 EndZ=0
    g262: LineSegment StartX=21.9956 StartY=37.75 StartZ=0 EndX=9.99111 EndY=37.75 EndZ=0
    g263: ArcOfCircle CenterX=-7.3e-15 CenterY=0 CenterZ=0 NormalX=0 NormalY=0 NormalZ=1 AngleXU=0 Radius=37.75 StartAngle=1.6238 EndAngle=1.91439
    g264: LineSegment StartX=-10.98 StartY=32.5354 StartZ=0 EndX=-4.98002 EndY=32.5354 EndZ=0
    g265: LineSegment StartX=-10.98 StartY=32.5354 StartZ=0 EndX=-12.7168 EndY=35.5436 EndZ=0
    g266: LineSegment StartX=-4.98002 StartY=32.5354 StartZ=0 EndX=-2 EndY=37.697 EndZ=0
    g267: LineSegment StartX=-22.6407 StartY=25.293 StartZ=0 EndX=-24.5797 EndY=28.6514 EndZ=0
    g268: ArcOfCircle CenterX=-7.3e-15 CenterY=0 CenterZ=0 NormalX=0 NormalY=0 NormalZ=1 AngleXU=0 Radius=37.75 StartAngle=2.00337 EndAngle=2.27985
    g269: LineSegment StartX=45.9816 StartY=-17.6631 StartZ=0 EndX=42.9816 EndY=-12.4669 EndZ=0
    g270: LineSegment StartX=42.9816 StartY=-12.4669 StartZ=0 EndX=36.9816 EndY=-12.4669 EndZ=0
    g271: LineSegment StartX=36.9816 StartY=-12.4669 StartZ=0 EndX=33.9816 EndY=-17.6631 EndZ=0
    g272: LineSegment StartX=33.9816 StartY=-17.6631 StartZ=0 EndX=36.9816 EndY=-22.8592 EndZ=0
    g273: LineSegment StartX=36.9816 StartY=-22.8592 StartZ=0 EndX=42.9816 EndY=-22.8592 EndZ=0
    g274: LineSegment StartX=42.9816 StartY=-22.8592 StartZ=0 EndX=45.9816 EndY=-17.6631 EndZ=0
    g275: Circle [constr] CenterX=39.9816 CenterY=-17.6631 CenterZ=0 NormalX=0 NormalY=0 NormalZ=1 AngleXU=0 Radius=6
    g276: LineSegment StartX=46.0022 StartY=-3.81076 StartZ=0 EndX=43.0022 EndY=1.38539 EndZ=0
    g277: LineSegment StartX=43.0022 StartY=1.38539 StartZ=0 EndX=37.0022 EndY=1.38539 EndZ=0
    g278: LineSegment StartX=37.0022 StartY=1.38539 StartZ=0 EndX=34.0022 EndY=-3.81076 EndZ=0
    g279: LineSegment StartX=34.0022 StartY=-3.81076 StartZ=0 EndX=37.0022 EndY=-9.00691 EndZ=0
    g280: LineSegment StartX=37.0022 StartY=-9.00691 StartZ=0 EndX=43.0022 EndY=-9.00691 EndZ=0
    g281: LineSegment StartX=43.0022 StartY=-9.00691 StartZ=0 EndX=46.0022 EndY=-3.81076 EndZ=0
    g282: Circle [constr] CenterX=40.0022 CenterY=-3.81076 CenterZ=0 NormalX=0 NormalY=0 NormalZ=1 AngleXU=0 Radius=6
    g283: LineSegment StartX=33.8871 StartY=-10.7331 StartZ=0 EndX=30.8871 EndY=-5.53691 EndZ=0
    g284: LineSegment StartX=30.8871 StartY=-5.53691 StartZ=0 EndX=24.8871 EndY=-5.53691 EndZ=0
    g285: LineSegment StartX=24.8871 StartY=-5.53691 StartZ=0 EndX=21.8871 EndY=-10.7331 EndZ=0
    g286: LineSegment StartX=21.8871 StartY=-10.7331 StartZ=0 EndX=24.8871 EndY=-15.9292 EndZ=0
    g287: LineSegment StartX=24.8871 StartY=-15.9292 StartZ=0 EndX=30.8871 EndY=-15.9292 EndZ=0
    g288: LineSegment StartX=30.8871 StartY=-15.9292 StartZ=0 EndX=33.8871 EndY=-10.7331 EndZ=0
    g289: Circle [constr] CenterX=27.8871 CenterY=-10.7331 CenterZ=0 NormalX=0 NormalY=0 NormalZ=1 AngleXU=0 Radius=6
    g290: LineSegment StartX=33.8105 StartY=-24.5854 StartZ=0 EndX=30.8105 EndY=-19.3892 EndZ=0
    g291: LineSegment StartX=30.8105 StartY=-19.3892 StartZ=0 EndX=24.8105 EndY=-19.3892 EndZ=0
    g292: LineSegment StartX=24.8105 StartY=-19.3892 StartZ=0 EndX=21.8105 EndY=-24.5854 EndZ=0
    g293: LineSegment StartX=21.8105 StartY=-24.5854 StartZ=0 EndX=24.8105 EndY=-29.7815 EndZ=0
    g294: LineSegment StartX=24.8105 StartY=-29.7815 StartZ=0 EndX=30.8105 EndY=-29.7815 EndZ=0
    g295: LineSegment StartX=30.8105 StartY=-29.7815 StartZ=0 EndX=33.8105 EndY=-24.5854 EndZ=0
    g296: Circle [constr] CenterX=27.8105 CenterY=-24.5854 CenterZ=0 NormalX=0 NormalY=0 NormalZ=1 AngleXU=0 Radius=6
    g297: LineSegment StartX=22 StartY=-31.5154 StartZ=0 EndX=19 EndY=-26.3192 EndZ=0
    g298: LineSegment StartX=19 StartY=-26.3192 StartZ=0 EndX=13 EndY=-26.3192 EndZ=0
    g299: LineSegment StartX=13 StartY=-26.3192 StartZ=0 EndX=9.99999 EndY=-31.5154 EndZ=0
    g300: LineSegment StartX=9.99999 StartY=-31.5154 StartZ=0 EndX=13 EndY=-36.7115 EndZ=0
    g301: LineSegment StartX=13 StartY=-36.7115 StartZ=0 EndX=19 EndY=-36.7115 EndZ=0
    g302: LineSegment StartX=19 StartY=-36.7115 StartZ=0 EndX=22 EndY=-31.5154 EndZ=0
    g303: Circle [constr] CenterX=16 CenterY=-31.5154 CenterZ=0 NormalX=0 NormalY=0 NormalZ=1 AngleXU=0 Radius=6
    g304: LineSegment StartX=-26.1895 StartY=-24.9201 StartZ=0 EndX=-23.5374 EndY=-29.5136 EndZ=0
    g305: LineSegment StartX=-17.1895 StartY=-30.1162 StartZ=0 EndX=-22.7613 EndY=-30.1162 EndZ=0
    g306: LineSegment StartX=46 StartY=-31.5154 StartZ=0 EndX=43 EndY=-26.3192 EndZ=0
    g307: LineSegment StartX=43 StartY=-26.3192 StartZ=0 EndX=37 EndY=-26.3192 EndZ=0
    g308: LineSegment StartX=37 StartY=-26.3192 StartZ=0 EndX=34 EndY=-31.5154 EndZ=0
    g309: LineSegment StartX=34 StartY=-31.5154 StartZ=0 EndX=37 EndY=-36.7115 EndZ=0
    g310: LineSegment StartX=37 StartY=-36.7115 StartZ=0 EndX=43 EndY=-36.7115 EndZ=0
    g311: LineSegment StartX=43 StartY=-36.7115 StartZ=0 EndX=46 EndY=-31.5154 EndZ=0
    g312: Circle [constr] CenterX=40 CenterY=-31.5154 CenterZ=0 NormalX=0 NormalY=0 NormalZ=1 AngleXU=0 Radius=6
    g313: LineSegment StartX=25.0189 StartY=-33.2415 StartZ=0 EndX=31.0189 EndY=-33.2415 EndZ=0
    g314: LineSegment StartX=25.0189 StartY=-33.2415 StartZ=0 EndX=22.4159 EndY=-37.75 EndZ=0
    g315: LineSegment StartX=31.0189 StartY=-33.2415 StartZ=0 EndX=33.6218 EndY=-37.75 EndZ=0
    g316: LineSegment StartX=22.4159 StartY=-37.75 StartZ=0 EndX=33.6218 EndY=-37.75 EndZ=0
    g317: ArcOfCircle CenterX=-1.08e-14 CenterY=3.25e-14 CenterZ=0 NormalX=0 NormalY=0 NormalZ=1 AngleXU=0 Radius=37.75 StartAngle=2.37833 EndAngle=2.62374
    g318: ArcOfCircle CenterX=7.8e-15 CenterY=2.85e-14 CenterZ=0 NormalX=0 NormalY=0 NormalZ=1 AngleXU=0 Radius=37.75 StartAngle=2.72641 EndAngle=2.92286
    g319: ArcOfCircle CenterX=4.5e-15 CenterY=-1.26e-14 CenterZ=0 NormalX=0 NormalY=0 NormalZ=1 AngleXU=0 Radius=37.75 StartAngle=3.22547 EndAngle=3.26845
    g320: ArcOfCircle CenterX=-1.13e-14 CenterY=2.26e-14 CenterZ=0 NormalX=0 NormalY=0 NormalZ=1 AngleXU=0 Radius=37.75 StartAngle=3.49677 EndAngle=3.7924
    g321: ArcOfCircle CenterX=-1.388e-13 CenterY=1.156e-13 CenterZ=0 NormalX=0 NormalY=0 NormalZ=1 AngleXU=0 Radius=37.75 StartAngle=4.03917 EndAngle=4.0652
    g322: ArcOfCircle CenterX=-1.08e-14 CenterY=3.25e-14 CenterZ=0 NormalX=0 NormalY=0 NormalZ=1 AngleXU=0 Radius=37.75 StartAngle=4.40471 EndAngle=4.47895
    g323: LineSegment StartX=9.62182 StartY=-37.75 StartZ=0 EndX=0 EndY=-37.75 EndZ=0
    g324: ArcOfCircle CenterX=-2.9e-15 CenterY=4.5e-15 CenterZ=0 NormalX=0 NormalY=0 NormalZ=1 AngleXU=0 Radius=37.75 StartAngle=4.67091 EndAngle=4.71239
    g325: LineSegment StartX=82.0044 StartY=37.75 StartZ=0 EndX=92 EndY=37.75 EndZ=0
    g326: ArcOfCircle CenterX=91.9985 CenterY=28.24 CenterZ=0 NormalX=0 NormalY=0 NormalZ=1 AngleXU=0 Radius=9.51 StartAngle=1.36968 EndAngle=1.57064
    g327: LineSegment StartX=103.902 StartY=26.6406 StartZ=0 EndX=100.219 EndY=33.0085 EndZ=0
    g328: LineSegment StartX=58 StartY=3.11924 StartZ=0 EndX=55 EndY=8.31539 EndZ=0
    g329: LineSegment StartX=55 StartY=8.31539 StartZ=0 EndX=49 EndY=8.31539 EndZ=0
    g330: LineSegment StartX=49 StartY=8.31539 StartZ=0 EndX=46 EndY=3.11924 EndZ=0
    g331: LineSegment StartX=46 StartY=3.11924 StartZ=0 EndX=49 EndY=-2.07691 EndZ=0
    g332: LineSegment StartX=49 StartY=-2.07691 StartZ=0 EndX=55 EndY=-2.07691 EndZ=0
    g333: LineSegment StartX=55 StartY=-2.07691 StartZ=0 EndX=58 EndY=3.11924 EndZ=0
    g334: Circle [constr] CenterX=52 CenterY=3.11924 CenterZ=0 NormalX=0 NormalY=0 NormalZ=1 AngleXU=0 Radius=6
    g335: LineSegment StartX=57.8871 StartY=-10.7331 StartZ=0 EndX=54.8871 EndY=-5.53691 EndZ=0
    g336: LineSegment StartX=54.8871 StartY=-5.53691 StartZ=0 EndX=48.8871 EndY=-5.53691 EndZ=0
    g337: LineSegment StartX=48.8871 StartY=-5.53691 StartZ=0 EndX=45.8871 EndY=-10.7331 EndZ=0
    g338: LineSegment StartX=45.8871 StartY=-10.7331 StartZ=0 EndX=48.8871 EndY=-15.9292 EndZ=0
    g339: LineSegment StartX=48.8871 StartY=-15.9292 StartZ=0 EndX=54.8871 EndY=-15.9292 EndZ=0
    g340: LineSegment StartX=54.8871 StartY=-15.9292 StartZ=0 EndX=57.8871 EndY=-10.7331 EndZ=0
    g341: Circle [constr] CenterX=51.8871 CenterY=-10.7331 CenterZ=0 NormalX=0 NormalY=0 NormalZ=1 AngleXU=0 Radius=6
    g342: LineSegment StartX=57.8105 StartY=-24.5854 StartZ=0 EndX=54.8105 EndY=-19.3892 EndZ=0
    g343: LineSegment StartX=54.8105 StartY=-19.3892 StartZ=0 EndX=48.8105 EndY=-19.3892 EndZ=0
    g344: LineSegment StartX=48.8105 StartY=-19.3892 StartZ=0 EndX=45.8105 EndY=-24.5854 EndZ=0
    g345: LineSegment StartX=45.8105 StartY=-24.5854 StartZ=0 EndX=48.8105 EndY=-29.7815 EndZ=0
    g346: LineSegment StartX=48.8105 StartY=-29.7815 StartZ=0 EndX=54.8105 EndY=-29.7815 EndZ=0
    g347: LineSegment StartX=54.8105 StartY=-29.7815 StartZ=0 EndX=57.8105 EndY=-24.5854 EndZ=0
    g348: Circle [constr] CenterX=51.8105 CenterY=-24.5854 CenterZ=0 NormalX=0 NormalY=0 NormalZ=1 AngleXU=0 Radius=6
    g349: LineSegment StartX=70.0877 StartY=10.0415 StartZ=0 EndX=67.0877 EndY=15.2377 EndZ=0
    g350: LineSegment StartX=67.0877 StartY=15.2377 StartZ=0 EndX=61.0877 EndY=15.2377 EndZ=0
    g351: LineSegment StartX=61.0877 StartY=15.2377 StartZ=0 EndX=58.0877 EndY=10.0415 EndZ=0
    g352: LineSegment StartX=58.0877 StartY=10.0415 StartZ=0 EndX=61.0877 EndY=4.84539 EndZ=0
    g353: LineSegment StartX=61.0877 StartY=4.84539 StartZ=0 EndX=67.0877 EndY=4.84539 EndZ=0
    g354: LineSegment StartX=67.0877 StartY=4.84539 StartZ=0 EndX=70.0877 EndY=10.0415 EndZ=0
    g355: Circle [constr] CenterX=64.0877 CenterY=10.0415 CenterZ=0 NormalX=0 NormalY=0 NormalZ=1 AngleXU=0 Radius=6
    g356: LineSegment StartX=70.0022 StartY=-3.81076 StartZ=0 EndX=67.0022 EndY=1.38539 EndZ=0
    g357: LineSegment StartX=67.0022 StartY=1.38539 StartZ=0 EndX=61.0022 EndY=1.38539 EndZ=0
    g358: LineSegment StartX=61.0022 StartY=1.38539 StartZ=0 EndX=58.0022 EndY=-3.81076 EndZ=0
    g359: LineSegment StartX=58.0022 StartY=-3.81076 StartZ=0 EndX=61.0022 EndY=-9.00691 EndZ=0
    g360: LineSegment StartX=61.0022 StartY=-9.00691 StartZ=0 EndX=67.0022 EndY=-9.00691 EndZ=0
    g361: LineSegment StartX=67.0022 StartY=-9.00691 StartZ=0 EndX=70.0022 EndY=-3.81076 EndZ=0
    g362: Circle [constr] CenterX=64.0022 CenterY=-3.81076 CenterZ=0 NormalX=0 NormalY=0 NormalZ=1 AngleXU=0 Radius=6
    g363: LineSegment StartX=69.9816 StartY=-17.6631 StartZ=0 EndX=66.9816 EndY=-12.4669 EndZ=0
    g364: LineSegment StartX=66.9816 StartY=-12.4669 StartZ=0 EndX=60.9816 EndY=-12.4669 EndZ=0
    g365: LineSegment StartX=60.9816 StartY=-12.4669 StartZ=0 EndX=57.9816 EndY=-17.6631 EndZ=0
    g366: LineSegment StartX=57.9816 StartY=-17.6631 StartZ=0 EndX=60.9816 EndY=-22.8592 EndZ=0
    g367: LineSegment StartX=60.9816 StartY=-22.8592 StartZ=0 EndX=66.9816 EndY=-22.8592 EndZ=0
    g368: LineSegment StartX=66.9816 StartY=-22.8592 StartZ=0 EndX=69.9816 EndY=-17.6631 EndZ=0
    g369: Circle [constr] CenterX=63.9816 CenterY=-17.6631 CenterZ=0 NormalX=0 NormalY=0 NormalZ=1 AngleXU=0 Radius=6
    g370: LineSegment StartX=70 StartY=-31.5154 StartZ=0 EndX=67 EndY=-26.3192 EndZ=0
    g371: LineSegment StartX=67 StartY=-26.3192 StartZ=0 EndX=61 EndY=-26.3192 EndZ=0
    g372: LineSegment StartX=61 StartY=-26.3192 StartZ=0 EndX=58 EndY=-31.5154 EndZ=0
    g373: LineSegment StartX=58 StartY=-31.5154 StartZ=0 EndX=61 EndY=-36.7115 EndZ=0
    g374: LineSegment StartX=61 StartY=-36.7115 StartZ=0 EndX=67 EndY=-36.7115 EndZ=0
    g375: LineSegment StartX=67 StartY=-36.7115 StartZ=0 EndX=70 EndY=-31.5154 EndZ=0
    g376: Circle [constr] CenterX=64 CenterY=-31.5154 CenterZ=0 NormalX=0 NormalY=0 NormalZ=1 AngleXU=0 Radius=6
    g377: LineSegment StartX=81.9973 StartY=16.9715 StartZ=0 EndX=78.9973 EndY=22.1677 EndZ=0
    g378: LineSegment StartX=78.9973 StartY=22.1677 StartZ=0 EndX=72.9973 EndY=22.1677 EndZ=0
    g379: LineSegment StartX=72.9973 StartY=22.1677 StartZ=0 EndX=69.9973 EndY=16.9715 EndZ=0
    g380: LineSegment StartX=69.9973 StartY=16.9715 StartZ=0 EndX=72.9973 EndY=11.7754 EndZ=0
    g381: LineSegment StartX=72.9973 StartY=11.7754 StartZ=0 EndX=78.9973 EndY=11.7754 EndZ=0
    g382: LineSegment StartX=78.9973 StartY=11.7754 StartZ=0 EndX=81.9973 EndY=16.9715 EndZ=0
    g383: Circle [constr] CenterX=75.9973 CenterY=16.9715 CenterZ=0 NormalX=0 NormalY=0 NormalZ=1 AngleXU=0 Radius=6
    g384: LineSegment StartX=82 StartY=3.11924 StartZ=0 EndX=79 EndY=8.31539 EndZ=0
    g385: LineSegment StartX=79 StartY=8.31539 StartZ=0 EndX=73 EndY=8.31539 EndZ=0
    g386: LineSegment StartX=73 StartY=8.31539 StartZ=0 EndX=70 EndY=3.11924 EndZ=0
    g387: LineSegment StartX=70 StartY=3.11924 StartZ=0 EndX=73 EndY=-2.07691 EndZ=0
    g388: LineSegment StartX=73 StartY=-2.07691 StartZ=0 EndX=79 EndY=-2.07691 EndZ=0
    g389: LineSegment StartX=79 StartY=-2.07691 StartZ=0 EndX=82 EndY=3.11924 EndZ=0
    g390: Circle [constr] CenterX=76 CenterY=3.11924 CenterZ=0 NormalX=0 NormalY=0 NormalZ=1 AngleXU=0 Radius=6
    g391: LineSegment StartX=81.8871 StartY=-10.7331 StartZ=0 EndX=78.8871 EndY=-5.53691 EndZ=0
    g392: LineSegment StartX=78.8871 StartY=-5.53691 StartZ=0 EndX=72.8871 EndY=-5.53691 EndZ=0
    g393: LineSegment StartX=72.8871 StartY=-5.53691 StartZ=0 EndX=69.8871 EndY=-10.7331 EndZ=0
    g394: LineSegment StartX=69.8871 StartY=-10.7331 StartZ=0 EndX=72.8871 EndY=-15.9292 EndZ=0
    g395: LineSegment StartX=72.8871 StartY=-15.9292 StartZ=0 EndX=78.8871 EndY=-15.9292 EndZ=0
    g396: LineSegment StartX=78.8871 StartY=-15.9292 StartZ=0 EndX=81.8871 EndY=-10.7331 EndZ=0
    g397: Circle [constr] CenterX=75.8871 CenterY=-10.7331 CenterZ=0 NormalX=0 NormalY=0 NormalZ=1 AngleXU=0 Radius=6
    g398: LineSegment StartX=81.8105 StartY=-24.5854 StartZ=0 EndX=78.8105 EndY=-19.3892 EndZ=0
    g399: LineSegment StartX=78.8105 StartY=-19.3892 StartZ=0 EndX=72.8105 EndY=-19.3892 EndZ=0
    ... +63 more geometry lines
  constraints (1185):
    c: Coincident(g5,g2)
    c: Coincident(g5,g3)
    c: Coincident(g5,g4)
    c: Vertical(g4,g3)
    c: Coincident(g0,g1)
    c: Coincident(g1,g7)
    c: Horizontal(g7)
    c: Horizontal(g6)
    c: Coincident(g1,g6)
    c: Vertical(g1,g0)
    c: Vertical(g0,g1)
    c: Coincident(g0,g-1)
    c: DistanceY(g1,g1) = 79.5
    c: Diameter(g5) = 29.5
    c: DistanceX(g4,g2) = 2.5
    c: PointOnObject(g2,g-1)
    c: PointOnObject(g8,g6)
    c: PointOnObject(g10,g7)
    c: Tangent(g7,g9) = -1.5708
    c: Vertical(g10,g8)
    c: DistanceX(g10,g2) = 15
    c: DistanceX(g7,g7) = 92
    c: Coincident(g11,g0)
    c: PointOnObject(g11,g-2)
    c: PointOnObject(g11,g-2)
    c: DistanceY(g1,g11) = 2
    c: Coincident(g12,g11)
    c: Horizontal(g12)
    c: Radius(g14) = 20
    c: Coincident(g14,g2)
    c: Coincident(g14,g13)
    c: PointOnObject(g16,g12)
    c: PointOnObject(g16,g13)
    c: Tangent(g12,g15) = 1.5708
    c: Tangent(g13,g15) = 1.5708
    c: Coincident(g17,g11)
    c: Horizontal(g17)
    c: Coincident(g18,g14)
    c: PointOnObject(g20,g17)
    c: PointOnObject(g20,g18)
    c: Tangent(g17,g19) = -1.5708
    c: Tangent(g18,g19) = -1.5708
    c: Coincident(g21,g7)
    c: Coincident(g21,g17)
    c: Vertical(g21)
    c: Distance(g22) = 6.5
    c: Coincident(g22,g3)
    c: Coincident(g23,g22)
    c: Coincident(g24,g6)
    c: Radius(g24) = 13.5
    c: Horizontal(g13,g23)
    c: Vertical(g6,g12)
    c: Vertical(g17,g12)
    c: Tangent(g24,g23) = -1.5708
    c: Coincident(g25,g4)
    c: Vertical(g25)
    c: Equal(g25,g22)
    c: Vertical(g22)
    c: Coincident(g26,g25)
    c: Equal(g9,g24)
    c: Vertical(g14,g13)
    c: DistanceX(g7,g25) = 18.61
    c: Tangent(g26,g9) = -1.5708
    c: Parallel(g18,g26)
    c: Parallel(g23,g13)
    c: Vertical(g24,g15)
    c: Coincident(g27,g28)
    c: Coincident(g28,g29)
    c: Coincident(g29,g30)
    c: Coincident(g30,g31)
    c: Coincident(g31,g32)
    c: Coincident(g32,g27)
    c: Equal(g27, g28-g32) x5
    c: PointOnObject(g27,g33)
    c: PointOnObject(g28,g33)
    c: PointOnObject(g29,g33)
    c: PointOnObject(g30,g33)
    c: PointOnObject(g31,g33)
    c: PointOnObject(g32,g33)
    c: Radius(g33) = 6
    c: Parallel(g28,g12)
    c: Distance(g34) = 6
    c: Horizontal(g34)
    c: Coincident(g35,g34)
    c: PointOnObject(g35,g12)
    c: Coincident(g36,g34)
    c: PointOnObject(g36,g12)
    c: Distance(g37) = 6
    c: Horizontal(g37)
    c: Coincident(g38,g37)
    c: PointOnObject(g38,g12)
    c: Coincident(g39,g37)
    c: Symmetric(g12,g12,g39)
    c: Distance(g40) = 6
    c: Horizontal(g40)
    c: Coincident(g41,g40)
    c: PointOnObject(g41,g12)
    c: Coincident(g42,g40)
    c: PointOnObject(g42,g12)
    c: Distance(g43) = 6
    c: Horizontal(g43)
    c: Coincident(g44,g43)
    c: PointOnObject(g44,g12)
    c: Coincident(g45,g43)
    c: PointOnObject(g45,g15)
    c: Distance(g46) = 6
    c: Distance(g47) = 6
    c: Coincident(g47,g46)
    c: Horizontal(g47)
    c: Distance(g48) = 6
    c: Coincident(g48,g46)
    c: PointOnObject(g48,g15)
    c: Coincident(g49,g47)
    c: PointOnObject(g49,g13)
    c: Distance(g50) = 6
    c: Horizontal(g50)
    c: Distance(g51) = 6
    c: Coincident(g51,g50)
    c: Coincident(g52,g51)
    c: PointOnObject(g52,g11)
    c: Distance(g53) = 6
    c: Coincident(g54,g53)
    c: PointOnObject(g54,g11)
    c: Horizontal(g54)
    c: Coincident(g55,g53)
    c: PointOnObject(g55,g11)
    c: Distance(g56) = 6
    c: Horizontal(g56)
    c: Distance(g57) = 6
    c: Coincident(g57,g56)
    c: Distance(g58) = 6
    c: Coincident(g58,g57)
    c: Coincident(g59,g58)
    c: PointOnObject(g59,g11)
    c: Horizontal(g59)
    c: Coincident(g60,g56)
    c: PointOnObject(g60,g11)
    c: Distance(g61) = 6
    c: Horizontal(g61)
    c: Distance(g62) = 6
    c: Coincident(g62,g61)
    c: Distance(g63) = 6
    c: Coincident(g63,g62)
    c: Distance(g64) = 6
    c: Coincident(g64,g63)
    c: Horizontal(g64)
    c: Coincident(g65,g64)
    c: PointOnObject(g65,g11)
    c: Coincident(g66,g61)
    c: PointOnObject(g66,g11)
    c: Distance(g67) = 6
    c: Horizontal(g67)
    c: Distance(g68) = 6
    c: Coincident(g68,g67)
    c: Distance(g69) = 6
    c: Coincident(g69,g68)
    c: Coincident(g70,g69)
    c: PointOnObject(g70,g11)
    c: Horizontal(g70)
    c: Coincident(g71,g67)
    c: PointOnObject(g71,g11)
    c: Distance(g72) = 6
    c: Horizontal(g72)
    c: Distance(g73) = 6
    c: Coincident(g73,g72)
    c: Distance(g74) = 6
    c: Coincident(g74,g73)
    c: Distance(g75) = 6
    c: Coincident(g75,g72)
    c: Distance(g76) = 6
    c: Horizontal(g76)
    c: Distance(g77) = 6
    c: Coincident(g77,g76)
    c: Coincident(g78,g77)
    c: PointOnObject(g78,g11)
    c: Distance(g79) = 6
    c: Coincident(g79,g76)
    c: Distance(g80) = 6
    c: Coincident(g80,g79)
    c: Coincident(g81,g80)
    c: PointOnObject(g81,g11)
    c: Coincident(g82,g83)
    c: Coincident(g83,g84)
    c: Coincident(g84,g85)
    c: Coincident(g85,g86)
    c: Coincident(g86,g87)
    c: Coincident(g87,g82)
    c: Equal(g82, g83-g87) x5
    c: PointOnObject(g82,g88)
    c: PointOnObject(g83,g88)
    c: PointOnObject(g84,g88)
    c: PointOnObject(g85,g88)
    c: PointOnObject(g86,g88)
    c: PointOnObject(g87,g88)
    c: Radius(g88) = 6
    c: Coincident(g89,g90)
    c: Coincident(g90,g91)
    c: Coincident(g91,g92)
    c: Coincident(g92,g93)
    c: Coincident(g93,g94)
    c: Coincident(g94,g89)
    c: Equal(g89, g90-g94) x5
    c: PointOnObject(g89,g95)
    c: PointOnObject(g90,g95)
    c: PointOnObject(g91,g95)
    c: PointOnObject(g92,g95)
    c: PointOnObject(g93,g95)
    c: PointOnObject(g94,g95)
    c: Radius(g95) = 6
    c: Coincident(g96,g97)
    c: Coincident(g97,g98)
    c: Coincident(g98,g99)
    c: Coincident(g99,g100)
    c: Coincident(g100,g101)
    c: Coincident(g101,g96)
    c: Equal(g96, g97-g101) x5
    c: PointOnObject(g96,g102)
    c: PointOnObject(g97,g102)
    c: PointOnObject(g98,g102)
    c: PointOnObject(g99,g102)
    c: PointOnObject(g100,g102)
    c: PointOnObject(g101,g102)
    c: Radius(g102) = 6
    c: Coincident(g103,g104)
    c: Coincident(g104,g105)
    c: Coincident(g105,g106)
    c: Coincident(g106,g107)
    c: Coincident(g107,g108)
    c: Coincident(g108,g103)
    c: Equal(g103, g104-g108) x5
    c: PointOnObject(g103,g109)
    c: PointOnObject(g104,g109)
    c: PointOnObject(g105,g109)
    c: PointOnObject(g106,g109)
    c: PointOnObject(g107,g109)
    c: PointOnObject(g108,g109)
    c: Radius(g109) = 6
    c: Coincident(g110,g111)
    c: Coincident(g111,g112)
    c: Coincident(g112,g113)
    c: Coincident(g113,g114)
    c: Coincident(g114,g115)
    c: Coincident(g115,g110)
    c: Equal(g110, g111-g115) x5
    c: PointOnObject(g110,g116)
    c: PointOnObject(g111,g116)
    c: PointOnObject(g112,g116)
    c: PointOnObject(g113,g116)
    c: PointOnObject(g114,g116)
    c: PointOnObject(g115,g116)
    c: Radius(g116) = 6
    c: Coincident(g117,g118)
    c: Coincident(g118,g119)
    c: Coincident(g119,g120)
    c: Coincident(g120,g121)
    c: Coincident(g121,g122)
    c: Coincident(g122,g117)
    c: Equal(g117, g118-g122) x5
    c: PointOnObject(g117,g123)
    c: PointOnObject(g118,g123)
    c: PointOnObject(g119,g123)
    c: PointOnObject(g120,g123)
    c: PointOnObject(g121,g123)
    c: PointOnObject(g122,g123)
    c: Radius(g123) = 6
    c: Coincident(g124,g125)
    c: Coincident(g125,g126)
    c: Coincident(g126,g127)
    c: Coincident(g127,g128)
    c: Coincident(g128,g129)
    c: Coincident(g129,g124)
    c: Equal(g124, g125-g129) x5
    c: PointOnObject(g124,g130)
    c: PointOnObject(g125,g130)
    c: PointOnObject(g126,g130)
    c: PointOnObject(g127,g130)
    c: PointOnObject(g128,g130)
    c: PointOnObject(g129,g130)
    c: Radius(g130) = 6
    c: Coincident(g131,g132)
    c: Coincident(g132,g133)
    c: Coincident(g133,g134)
    c: Coincident(g134,g135)
    c: Coincident(g135,g136)
    c: Coincident(g136,g131)
    c: Equal(g131, g132-g136) x5
    c: PointOnObject(g131,g137)
    c: PointOnObject(g132,g137)
    c: PointOnObject(g133,g137)
    c: PointOnObject(g134,g137)
    c: PointOnObject(g135,g137)
    c: PointOnObject(g136,g137)
    c: Radius(g137) = 6
    c: Coincident(g138,g139)
    c: Coincident(g139,g140)
    c: Coincident(g140,g141)
    c: Coincident(g141,g142)
    c: Coincident(g142,g143)
    c: Coincident(g143,g138)
    c: Equal(g138, g139-g143) x5
    c: PointOnObject(g138,g144)
    c: PointOnObject(g139,g144)
    c: PointOnObject(g140,g144)
    c: PointOnObject(g141,g144)
    c: PointOnObject(g142,g144)
    c: PointOnObject(g143,g144)
    c: Radius(g144) = 6
    c: Coincident(g145,g146)
    c: Coincident(g146,g147)
    c: Coincident(g147,g148)
    c: Coincident(g148,g149)
    c: Coincident(g149,g150)
    c: Coincident(g150,g145)
    c: Equal(g145, g146-g150) x5
    c: PointOnObject(g145,g151)
    c: PointOnObject(g146,g151)
    c: PointOnObject(g147,g151)
    c: PointOnObject(g148,g151)
    c: PointOnObject(g149,g151)
    c: PointOnObject(g150,g151)
    c: Radius(g151) = 6
    c: Coincident(g152,g153)
    c: Coincident(g153,g154)
    c: Coincident(g154,g155)
    c: Coincident(g155,g156)
    c: Coincident(g156,g157)
    c: Coincident(g157,g152)
    c: Equal(g152, g153-g157) x5
    c: PointOnObject(g152,g158)
    c: PointOnObject(g153,g158)
    c: PointOnObject(g154,g158)
    c: PointOnObject(g155,g158)
    c: PointOnObject(g156,g158)
    c: PointOnObject(g157,g158)
    c: Radius(g158) = 6
    c: Coincident(g159,g160)
    c: Coincident(g160,g161)
    c: Coincident(g161,g162)
    c: Coincident(g162,g163)
    c: Coincident(g163,g164)
    c: Coincident(g164,g159)
    c: Equal(g159, g160-g164) x5
    c: PointOnObject(g159,g165)
    c: PointOnObject(g160,g165)
    c: PointOnObject(g161,g165)
    c: PointOnObject(g162,g165)
    c: PointOnObject(g163,g165)
    c: PointOnObject(g164,g165)
    c: Radius(g165) = 6
    c: Coincident(g166,g167)
    c: Coincident(g167,g168)
    c: Coincident(g168,g169)
    c: Coincident(g169,g170)
    c: Coincident(g170,g171)
    c: Coincident(g171,g166)
    c: Equal(g166, g167-g171) x5
    c: PointOnObject(g166,g172)
    c: PointOnObject(g167,g172)
    c: PointOnObject(g168,g172)
    c: PointOnObject(g169,g172)
    c: PointOnObject(g170,g172)
    c: PointOnObject(g171,g172)
    c: Radius(g172) = 6
    c: Coincident(g173,g174)
    c: Coincident(g174,g175)
    c: Coincident(g175,g176)
    c: Coincident(g176,g177)
    c: Coincident(g177,g178)
    c: Coincident(g178,g173)
    c: Equal(g173, g174-g178) x5
    c: PointOnObject(g173,g179)
    c: PointOnObject(g174,g179)
    c: PointOnObject(g175,g179)
    c: PointOnObject(g176,g179)
    c: PointOnObject(g177,g179)
    c: PointOnObject(g178,g179)
    c: Radius(g179) = 6
    c: Coincident(g180,g181)
    c: Coincident(g181,g182)
    c: Coincident(g182,g183)
    c: Coincident(g183,g184)
    c: Coincident(g184,g185)
    c: Coincident(g185,g180)
    c: Equal(g180, g181-g185) x5
    c: PointOnObject(g180,g186)
    c: PointOnObject(g181,g186)
    c: PointOnObject(g182,g186)
    c: PointOnObject(g183,g186)
    c: PointOnObject(g184,g186)
    c: PointOnObject(g185,g186)
    c: Radius(g186) = 6
    c: Coincident(g187,g188)
    c: Coincident(g188,g189)
    c: Coincident(g189,g190)
    c: Coincident(g190,g191)
    c: Coincident(g191,g192)
    c: Coincident(g192,g187)
    c: Equal(g187, g188-g192) x5
    c: PointOnObject(g187,g193)
    c: PointOnObject(g188,g193)
    c: PointOnObject(g189,g193)
    c: PointOnObject(g190,g193)
    c: PointOnObject(g191,g193)
    c: PointOnObject(g192,g193)
    c: Radius(g193) = 6
    c: Coincident(g194,g195)
    c: Coincident(g195,g196)
    c: Coincident(g196,g197)
    c: Coincident(g197,g198)
    c: Coincident(g198,g199)
    c: Coincident(g199,g194)
    c: Equal(g194, g195-g199) x5
    c: PointOnObject(g194,g200)
    c: PointOnObject(g195,g200)
    c: PointOnObject(g196,g200)
    c: PointOnObject(g197,g200)
    c: PointOnObject(g198,g200)
    c: PointOnObject(g199,g200)
    c: Radius(g200) = 6
    c: Distance(g201) = 6
    c: Horizontal(g201)
    c: PointOnObject(g202,g11)
    c: Coincident(g203,g201)
    c: Coincident(g202,g201)
    c: Coincident(g204,g205)
    c: Coincident(g205,g206)
    c: Coincident(g206,g207)
    c: Coincident(g207,g208)
    c: Coincident(g208,g209)
    c: Coincident(g209,g204)
    c: Equal(g204, g205-g209) x5
    c: PointOnObject(g204,g210)
    c: PointOnObject(g205,g210)
    c: PointOnObject(g206,g210)
    c: PointOnObject(g207,g210)
    c: PointOnObject(g208,g210)
    c: PointOnObject(g209,g210)
    c: Radius(g210) = 6
    c: Coincident(g211,g212)
    c: Coincident(g212,g213)
    c: Coincident(g213,g214)
    c: Coincident(g214,g215)
    c: Coincident(g215,g216)
    c: Coincident(g216,g211)
    c: Equal(g211, g212-g216) x5
    c: PointOnObject(g211,g217)
    c: PointOnObject(g212,g217)
    c: PointOnObject(g213,g217)
    c: PointOnObject(g214,g217)
    c: PointOnObject(g215,g217)
    c: PointOnObject(g216,g217)
    c: Radius(g217) = 6
    c: Coincident(g218,g219)
    c: Coincident(g219,g220)
    c: Coincident(g220,g221)
    c: Coincident(g221,g222)
    c: Coincident(g222,g223)
    c: Coincident(g223,g218)
    c: Equal(g218, g219-g223) x5
    c: PointOnObject(g218,g224)
    c: PointOnObject(g219,g224)
    c: PointOnObject(g220,g224)
    c: PointOnObject(g221,g224)
    c: PointOnObject(g222,g224)
    c: PointOnObject(g223,g224)
    c: Radius(g224) = 6
    c: Coincident(g225,g226)
    c: Coincident(g226,g227)
    c: Coincident(g227,g228)
    c: Coincident(g228,g229)
    c: Coincident(g229,g230)
    c: Coincident(g230,g225)
    c: Equal(g225, g226-g230) x5
    c: PointOnObject(g225,g231)
    c: PointOnObject(g226,g231)
    c: PointOnObject(g227,g231)
    c: PointOnObject(g228,g231)
    c: PointOnObject(g229,g231)
    c: PointOnObject(g230,g231)
    c: Radius(g231) = 6
    c: Coincident(g232,g233)
    c: Coincident(g233,g234)
    c: Coincident(g234,g235)
    c: Coincident(g235,g236)
    c: Coincident(g236,g237)
    c: Coincident(g237,g232)
    c: Equal(g232, g233-g237) x5
    c: PointOnObject(g232,g238)
    c: PointOnObject(g233,g238)
    c: PointOnObject(g234,g238)
    c: PointOnObject(g235,g238)
    c: PointOnObject(g236,g238)
    c: PointOnObject(g237,g238)
    c: Radius(g238) = 6
    c: Coincident(g239,g240)
    c: Coincident(g240,g241)
    c: Coincident(g241,g242)
    c: Coincident(g242,g243)
    c: Coincident(g243,g244)
    c: Coincident(g244,g239)
    c: Equal(g239, g240-g244) x5
    c: PointOnObject(g239,g245)
    c: PointOnObject(g240,g245)
    c: PointOnObject(g241,g245)
    c: PointOnObject(g242,g245)
    c: PointOnObject(g243,g245)
    c: PointOnObject(g244,g245)
    c: Radius(g245) = 6
    c: Coincident(g246,g247)
    c: Coincident(g247,g248)
    c: Coincident(g248,g249)
    c: Coincident(g249,g250)
    c: Coincident(g250,g251)
    c: Coincident(g251,g246)
    c: Equal(g246, g247-g251) x5
    c: PointOnObject(g246,g252)
    c: PointOnObject(g247,g252)
    c: PointOnObject(g248,g252)
    c: PointOnObject(g249,g252)
    c: PointOnObject(g250,g252)
    c: PointOnObject(g251,g252)
    c: Radius(g252) = 6
    c: Coincident(g253,g254)
    c: Coincident(g254,g255)
    c: Coincident(g255,g256)
    c: Coincident(g256,g257)
    c: Coincident(g257,g258)
    c: Coincident(g258,g253)
    c: Equal(g253, g254-g258) x5
    c: PointOnObject(g253,g259)
    c: PointOnObject(g254,g259)
    c: PointOnObject(g255,g259)
    c: PointOnObject(g256,g259)
    c: PointOnObject(g257,g259)
    c: PointOnObject(g258,g259)
    c: Radius(g259) = 6
    c: Coincident(g260,g42)
    c: Coincident(g260,g41)
    c: Coincident(g261,g39)
    c: Coincident(g261,g38)
    c: Coincident(g262,g36)
    c: Coincident(g262,g35)
    c: Coincident(g263,g11)
    c: PointOnObject(g263,g11)
    c: Distance(g264) = 6
    c: Horizontal(g264)
    c: Coincident(g265,g264)
    c: Coincident(g265,g263)
    c: Coincident(g266,g264)
    c: Coincident(g266,g263)
    c: DistanceX(g263,g11) = 2
    c: Coincident(g267,g50)
    c: Coincident(g268,g11)
    c: Coincident(g52,g268)
    c: Coincident(g267,g268)
    c: DistanceX(g27,g126) = 12
    c: DistanceX(g51,g29) = 12
    c: DistanceX(g124,g119) = 12
    c: DistanceX(g53,g147) = 12
    c: DistanceX(g145,g133) = 12
    c: DistanceX(g131,g91) = 12
    c: DistanceX(g152,g140) = 12
    c: DistanceX(g138,g220) = 12
    c: DistanceX(g57,g161) = 12
    c: Coincident(g269,g270)
    c: Coincident(g270,g271)
    c: Coincident(g271,g272)
    c: Coincident(g272,g273)
    c: Coincident(g273,g274)
    c: Coincident(g274,g269)
    c: Equal(g269, g270-g274) x5
    c: PointOnObject(g269,g275)
    c: PointOnObject(g270,g275)
    c: PointOnObject(g271,g275)
    c: PointOnObject(g272,g275)
    c: PointOnObject(g273,g275)
    c: PointOnObject(g274,g275)
    c: Radius(g275) = 6
    c: DistanceX(g239,g271) = 12
    c: Coincident(g276,g277)
    c: Coincident(g277,g278)
    c: Coincident(g278,g279)
    c: Coincident(g279,g280)
    c: Coincident(g280,g281)
    c: Coincident(g281,g276)
    c: Equal(g276, g277-g281) x5
    c: PointOnObject(g276,g282)
    c: PointOnObject(g277,g282)
    c: PointOnObject(g278,g282)
    c: PointOnObject(g279,g282)
    c: PointOnObject(g280,g282)
    c: PointOnObject(g281,g282)
    c: Radius(g282) = 6
    c: DistanceX(g232,g278) = 12
    c: DistanceX(g166,g206) = 12
    c: DistanceX(g204,g255) = 12
    c: DistanceX(g62,g182) = 12
    c: DistanceX(g180,g234) = 12
    c: DistanceY(g153,g50) = 3.46
    c: DistanceY(g72,g176) = 3.46
    c: DistanceY(g167,g155) = 3.46
    c: DistanceY(g166,g156) = 3.46
    c: DistanceY(g58,g53) = 3.46
    c: DistanceY(g61,g56) = 3.46
    c: DistanceY(g67,g63) = 3.46
    c: DistanceX(g68,g189) = 12
    c: DistanceY(g146,g264) = 3.46
    c: DistanceY(g160,g148) = 3.46
    c: DistanceY(g181,g162) = 3.46
    c: DistanceY(g188,g183) = 3.46
    c: DistanceY(g76,g190) = 3.46
    c: DistanceY(g76,g191) = 3.46
    c: DistanceY(g187,g184) = 3.46
    c: DistanceY(g180,g163) = 3.46
    c: DistanceY(g159,g149) = 3.46
    c: DistanceY(g139,g30) = 3.46
    c: DistanceY(g138,g31) = 3.46
    c: DistanceY(g205,g141) = 3.46
    c: DistanceX(g159,g213) = 12
    c: DistanceY(g204,g142) = 3.46
    c: DistanceY(g226,g207) = 3.46
    c: DistanceY(g225,g208) = 3.46
    c: DistanceX(g173,g227) = 12
    c: DistanceX(g187,g241) = 12
    c: DistanceY(g195,g228) = 3.46
    c: Horizontal(g195)
    c: DistanceY(g201,g197) = 3.46
    c: DistanceX(g73,g196) = 12
    c: Horizontal(g132)
    c: Horizontal(g212)
    c: Horizontal(g233)
    c: Horizontal(g240)
    c: DistanceY(g132,g34) = 3.46
    c: DistanceY(g212,g134) = 3.46
    c: DistanceY(g233,g214) = 3.46
    c: DistanceY(g240,g235) = 3.46
    c: DistanceY(g219,g127) = 3.46
    c: DistanceY(g254,g221) = 3.46
    c: Horizontal(g254)
    c: Coincident(g283,g284)
    c: Coincident(g284,g285)
    c: Coincident(g285,g286)
    c: Coincident(g286,g287)
    c: Coincident(g287,g288)
    c: Coincident(g288,g283)
    c: Equal(g283, g284-g288) x5
    c: PointOnObject(g283,g289)
    c: PointOnObject(g284,g289)
    c: PointOnObject(g285,g289)
    c: PointOnObject(g286,g289)
    c: PointOnObject(g287,g289)
    c: PointOnObject(g288,g289)
    c: Radius(g289) = 6
    c: Coincident(g290,g291)
    c: Coincident(g291,g292)
    c: Coincident(g292,g293)
    c: Coincident(g293,g294)
    c: Coincident(g294,g295)
    c: Coincident(g295,g290)
    c: Equal(g290, g291-g295) x5
    c: PointOnObject(g290,g296)
    c: PointOnObject(g291,g296)
    c: PointOnObject(g292,g296)
    c: PointOnObject(g293,g296)
    c: PointOnObject(g294,g296)
    c: PointOnObject(g295,g296)
    c: Radius(g296) = 6
    c: Coincident(g297,g298)
    c: Coincident(g298,g299)
    c: Coincident(g299,g300)
    c: Coincident(g300,g301)
    c: Coincident(g301,g302)
    c: Coincident(g302,g297)
    c: Equal(g297, g298-g302) x5
    c: PointOnObject(g297,g303)
    c: PointOnObject(g298,g303)
    c: PointOnObject(g299,g303)
    c: PointOnObject(g300,g303)
    c: PointOnObject(g301,g303)
    c: PointOnObject(g302,g303)
    c: Radius(g303) = 6
    c: DistanceX(g225,g285) = 12
    c: DistanceY(g298,g242) = 3.46
    c: DistanceX(g79,g299) = 12
    c: DistanceX(g194,g292) = 12
    c: DistanceY(g104,g42) = 1.73
    c: DistanceY(g118,g39) = 1.73
    c: DistanceY(g125,g36) = 1.73
    c: Horizontal(g273)
    c: Horizontal(g280)
    c: Horizontal(g250)
    c: Horizontal(g93)
    c: Horizontal(g128)
    c: Horizontal(g222)
    c: Horizontal(g287)
    c: Horizontal(g294)
    c: Horizontal(g301)
    c: Horizontal(g86)
    c: Horizontal(g121)
    c: Horizontal(g100)
    c: Horizontal(g107)
    c: Horizontal(g114)
    c: DistanceY(g284,g256) = 3.46
    c: DistanceY(g291,g286) = 3.46
    c: DistanceY(g90,g37) = 3.46
    c: DistanceY(g247,g92) = 3.46
    c: DistanceY(g277,g249) = 3.46
    c: DistanceY(g270,g279) = 3.46
    c: DistanceX(g211,g248) = 12
    c: DistanceX(g89,g98) = 12
    c: DistanceX(g117,g105) = 12
    c: DistanceX(g103,g46) = 12
    c: DistanceX(g96,g112) = 12
    c: DistanceX(g218,g84) = 12
    c: DistanceY(g83,g120) = 3.46
    c: DistanceY(g97,g40) = 3.46
    c: DistanceY(g111,g43) = 3.46
    c: DistanceY(g132,g35) = 8.66
    c: DistanceY(g97,g41) = 8.66
    c: DistanceY(g90,g38) = 8.66
    c: DistanceY(g111,g44) = 8.66
    c: Parallel(g52,g145)
    c: Parallel(g267,g148)
    c: Parallel(g266,g29)
    c: Parallel(g265,g148)
    c: Parallel(g55,g152)
    c: Parallel(g58,g152)
    c: Parallel(g60,g155)
    c: Parallel(g66,g168)
    c: Parallel(g62,g166)
    c: Parallel(g65,g169)
    c: Parallel(g68,g173)
    c: Parallel(g71,g175)
    c: Parallel(g75,g175)
    c: Parallel(g73,g173)
    c: Coincident(g304,g75)
    c: PointOnObject(g304,g11)
    c: Coincident(g305,g74)
    c: PointOnObject(g305,g11)
    c: Parallel(g177,g305)
    c: Parallel(g304,g176)
    c: Parallel(g77,g189)
    c: Parallel(g78,g190)
    c: Parallel(g81,g191)
    c: Parallel(g80,g192)
    c: Parallel(g79,g187)
    c: Parallel(g202,g196)
    c: Parallel(g203,g194)
    c: Parallel(g35,g27)
    c: Parallel(g36,g126)
    c: Parallel(g124,g38)
    c: Parallel(g119,g39)
    c: Parallel(g117,g41)
    c: Parallel(g105,g42)
    c: DistanceX(g39,g41) = 12
    c: DistanceX(g36,g38) = 12
    c: DistanceX(g42,g44) = 12
    c: DistanceY(g53,g50) = 1.41
    c: Block(g53)
    c: Coincident(g306,g307)
    c: Coincident(g307,g308)
    c: Coincident(g308,g309)
    c: Coincident(g309,g310)
    c: Coincident(g310,g311)
    c: Coincident(g311,g306)
    c: Equal(g306, g307-g311) x5
    c: PointOnObject(g306,g312)
    c: PointOnObject(g307,g312)
    c: PointOnObject(g308,g312)
    c: PointOnObject(g309,g312)
    c: PointOnObject(g310,g312)
    c: PointOnObject(g311,g312)
    c: Radius(g312) = 6
    c: Block(g80)
    c: Block(g74)
    c: DistanceX(g297,g308) = 12
    c: Horizontal(g310)
    c: DistanceY(g307,g272) = 3.46
    c: Block(g69)
    c: Block(g63)
    c: Block(g57)
    c: Block(g51)
    c: Distance(g313) = 6
    c: Horizontal(g313)
    c: Coincident(g314,g313)
    c: PointOnObject(g314,g17)
    c: Coincident(g315,g313)
    c: PointOnObject(g315,g17)
    c: Coincident(g316,g314)
    c: Coincident(g316,g315)
    c: Parallel(g314,g302)
    c: Parallel(g315,g309)
    c: Block(g203)
    c: DistanceY(g313,g293) = 3.46
    c: Block(g178)
    c: Block(g171)
    c: Block(g157)
    c: Block(g166)
    c: Block(g152)
    c: DistanceX(g201,g313) = 18
    c: DistanceX(g107,g46) = 18
    c: Parallel(g44,g103)
    c: Parallel(g45,g112)
    c: Parallel(g48,g112)
    c: Parallel(g49,g115)
    c: Coincident(g55,g317)
    c: Coincident(g317,g54)
    c: Coincident(g59,g318)
    c: Coincident(g318,g60)
    c: Radius(g318) = 37.75
    c: Coincident(g319,g66)
    c: Coincident(g319,g65)
    c: Radius(g319) = 37.75
    c: Coincident(g71,g320)
    c: Coincident(g320,g70)
    c: Radius(g320) = 37.75
    c: Coincident(g321,g304)
    c: Coincident(g305,g321)
    c: Coincident(g322,g317)
    c: Coincident(g322,g78)
    c: Coincident(g322,g81)
    c: Coincident(g323,g203)
    c: Tangent(g323,g11) = 1.5708
    c: Coincident(g202,g324)
    c: Radius(g324) = 37.75
    c: Coincident(g324,g17)
    c: Coincident(g325,g44)
    c: Coincident(g325,g12)
    c: Coincident(g45,g326)
    c: Radius(g326) = 9.51
    c: Coincident(g326,g12)
    c: Radius(g321) = 37.75
    c: Coincident(g327,g49)
    c: Coincident(g327,g13)
    c: Coincident(g328,g329)
    c: Coincident(g329,g330)
    c: Coincident(g330,g331)
    c: Coincident(g331,g332)
    c: Coincident(g332,g333)
    c: Coincident(g333,g328)
    c: Equal(g328, g329-g333) x5
    c: PointOnObject(g328,g334)
    c: PointOnObject(g329,g334)
    c: PointOnObject(g330,g334)
    c: PointOnObject(g331,g334)
    c: PointOnObject(g332,g334)
    c: PointOnObject(g333,g334)
    c: Radius(g334) = 6
    c: DistanceY(g329,g85) = 3.46
    c: Horizontal(g329)
    c: DistanceX(g253,g330) = 12
    c: Coincident(g335,g336)
    c: Coincident(g336,g337)
    c: Coincident(g337,g338)
    c: Coincident(g338,g339)
    c: Coincident(g339,g340)
    c: Coincident(g340,g335)
    c: Equal(g335, g336-g340) x5
    c: PointOnObject(g335,g341)
    c: PointOnObject(g336,g341)
    c: PointOnObject(g337,g341)
    c: PointOnObject(g338,g341)
    c: PointOnObject(g339,g341)
    c: PointOnObject(g340,g341)
    c: Radius(g341) = 6
    c: Coincident(g342,g343)
    c: Coincident(g343,g344)
    c: Coincident(g344,g345)
    c: Coincident(g345,g346)
    c: Coincident(g346,g347)
    c: Coincident(g347,g342)
    c: Equal(g342, g343-g347) x5
    c: PointOnObject(g342,g348)
    c: PointOnObject(g343,g348)
    c: PointOnObject(g344,g348)
    c: PointOnObject(g345,g348)
    c: PointOnObject(g346,g348)
    c: PointOnObject(g347,g348)
    c: Radius(g348) = 6
    c: Horizontal(g336)
    c: Horizontal(g343)
    c: DistanceY(g336,g331) = 3.46
    c: DistanceX(g283,g337) = 12
    c: DistanceY(g343,g338) = 3.46
    c: DistanceX(g290,g344) = 12
    c: Coincident(g349,g350)
    c: Coincident(g350,g351)
    c: Coincident(g351,g352)
    c: Coincident(g352,g353)
    c: Coincident(g353,g354)
    c: Coincident(g354,g349)
    c: Equal(g349, g350-g354) x5
    c: PointOnObject(g349,g355)
    c: PointOnObject(g350,g355)
    c: PointOnObject(g351,g355)
    c: PointOnObject(g352,g355)
    c: PointOnObject(g353,g355)
    c: PointOnObject(g354,g355)
    c: Radius(g355) = 6
    c: Coincident(g356,g357)
    c: Coincident(g357,g358)
    c: Coincident(g358,g359)
    c: Coincident(g359,g360)
    c: Coincident(g360,g361)
    c: Coincident(g361,g356)
    c: Equal(g356, g357-g361) x5
    c: PointOnObject(g356,g362)
    c: PointOnObject(g357,g362)
    c: PointOnObject(g358,g362)
    c: PointOnObject(g359,g362)
    c: PointOnObject(g360,g362)
    c: PointOnObject(g361,g362)
    c: Radius(g362) = 6
    c: Coincident(g363,g364)
    c: Coincident(g364,g365)
    c: Coincident(g365,g366)
    c: Coincident(g366,g367)
    c: Coincident(g367,g368)
    c: Coincident(g368,g363)
    c: Equal(g363, g364-g368) x5
    c: PointOnObject(g363,g369)
    c: PointOnObject(g364,g369)
    c: PointOnObject(g365,g369)
    c: PointOnObject(g366,g369)
    c: PointOnObject(g367,g369)
    c: PointOnObject(g368,g369)
    c: Radius(g369) = 6
    c: Coincident(g370,g371)
    c: Coincident(g371,g372)
    c: Coincident(g372,g373)
    c: Coincident(g373,g374)
    c: Coincident(g374,g375)
    c: Coincident(g375,g370)
    c: Equal(g370, g371-g375) x5
    c: PointOnObject(g370,g376)
    c: PointOnObject(g371,g376)
    c: PointOnObject(g372,g376)
    c: PointOnObject(g373,g376)
    c: PointOnObject(g374,g376)
    c: PointOnObject(g375,g376)
    c: Radius(g376) = 6
    c: Horizontal(g350)
    c: Horizontal(g357)
    c: Horizontal(g364)
    c: Horizontal(g371)
    c: DistanceX(g246,g351) = 12
    c: DistanceY(g350,g99) = 3.46
    c: DistanceY(g357,g352) = 3.46
    c: DistanceY(g364,g359) = 3.46
    c: DistanceY(g371,g366) = 3.46
    c: DistanceX(g276,g358) = 12
    c: DistanceX(g269,g365) = 12
    c: DistanceX(g306,g372) = 12
    c: Coincident(g377,g378)
    c: Coincident(g378,g379)
    c: Coincident(g379,g380)
    c: Coincident(g380,g381)
    c: Coincident(g381,g382)
    c: Coincident(g382,g377)
    c: Equal(g377, g378-g382) x5
    c: PointOnObject(g377,g383)
    c: PointOnObject(g378,g383)
    c: PointOnObject(g379,g383)
    c: PointOnObject(g380,g383)
    c: PointOnObject(g381,g383)
    c: PointOnObject(g382,g383)
    c: Radius(g383) = 6
    c: Coincident(g384,g385)
    c: Coincident(g385,g386)
    c: Coincident(g386,g387)
    c: Coincident(g387,g388)
    c: Coincident(g388,g389)
    c: Coincident(g389,g384)
    c: Equal(g384, g385-g389) x5
    c: PointOnObject(g384,g390)
    c: PointOnObject(g385,g390)
    c: PointOnObject(g386,g390)
    c: PointOnObject(g387,g390)
    c: PointOnObject(g388,g390)
    c: PointOnObject(g389,g390)
    c: Radius(g390) = 6
    c: Coincident(g391,g392)
    c: Coincident(g392,g393)
    c: Coincident(g393,g394)
    c: Coincident(g394,g395)
    c: Coincident(g395,g396)
    c: Coincident(g396,g391)
    c: Equal(g391, g392-g396) x5
    c: PointOnObject(g391,g397)
    c: PointOnObject(g392,g397)
    c: PointOnObject(g393,g397)
    c: PointOnObject(g394,g397)
    c: PointOnObject(g395,g397)
    c: PointOnObject(g396,g397)
    c: Radius(g397) = 6
    c: Coincident(g398,g399)
    c: Coincident(g399,g400)
    c: Coincident(g400,g401)
    c: Coincident(g401,g402)
    c: Coincident(g402,g403)
    c: Coincident(g403,g398)
    c: Equal(g398, g399-g403) x5
    c: PointOnObject(g398,g404)
    c: PointOnObject(g399,g404)
    c: PointOnObject(g400,g404)
    c: PointOnObject(g401,g404)
    c: PointOnObject(g402,g404)
    c: PointOnObject(g403,g404)
    c: Radius(g404) = 6
    c: DistanceY(g378,g106) = 3.46
    c: Horizontal(g378)
    c: Horizontal(g385)
    c: Horizontal(g392)
    c: Horizontal(g399)
    c: DistanceY(g385,g380) = 3.46
    c: DistanceY(g392,g387) = 3.46
    c: DistanceY(g399,g394) = 3.46
    c: DistanceX(g82,g379) = 12
    c: DistanceX(g328,g386) = 12
    c: DistanceX(g335,g393) = 12
    c: DistanceX(g342,g400) = 12
    c: Coincident(g405,g406)
    c: Coincident(g406,g407)
    c: Coincident(g407,g408)
    c: Coincident(g408,g409)
    c: Coincident(g409,g410)
    c: Coincident(g410,g405)
    c: Equal(g405, g406-g410) x5
    c: PointOnObject(g405,g411)
    c: PointOnObject(g406,g411)
    c: PointOnObject(g407,g411)
    c: PointOnObject(g408,g411)
    c: PointOnObject(g409,g411)
    c: PointOnObject(g410,g411)
    c: Radius(g411) = 6
    c: Coincident(g412,g413)
    c: Coincident(g413,g414)
    c: Coincident(g414,g415)
    c: Coincident(g415,g416)
    c: Coincident(g416,g417)
    c: Coincident(g417,g412)
    c: Equal(g412, g413-g417) x5
    c: PointOnObject(g412,g418)
    c: PointOnObject(g413,g418)
    c: PointOnObject(g414,g418)
    c: PointOnObject(g415,g418)
    c: PointOnObject(g416,g418)
    c: PointOnObject(g417,g418)
    c: Radius(g418) = 6
    c: Coincident(g419,g420)
    c: Coincident(g420,g421)
    c: Coincident(g421,g422)
    c: Coincident(g422,g423)
    c: Coincident(g423,g424)
    c: Coincident(g424,g419)
    c: Equal(g419, g420-g424) x5
    c: PointOnObject(g419,g425)
    c: PointOnObject(g420,g425)
    c: PointOnObject(g421,g425)
    c: PointOnObject(g422,g425)
    c: PointOnObject(g423,g425)
    c: PointOnObject(g424,g425)
    c: Radius(g425) = 6
    c: Horizontal(g420)
    c: Horizontal(g413)
    c: Horizontal(g406)
    c: DistanceX(g349,g407) = 12
    c: DistanceY(g406,g113) = 3.46
    c: DistanceX(g363,g414) = 12
    c: DistanceX(g370,g421) = 12
    c: DistanceY(g17,g423) = 1.04
    c: DistanceY(g420,g415) = 3.46
    c: Distance(g426) = 6
    c: Horizontal(g426)
    c: Coincident(g427,g426)
    c: PointOnObject(g427,g17)
    c: Coincident(g428,g426)
    c: Symmetric(g17,g17,g428)
    c: DistanceY(g426,g345) = 3.46
    c: Parallel(g311,g428)
    c: Parallel(g373,g427)
    c: Coincident(g429,g427)
    c: Coincident(g429,g428)
    c: Distance(g430) = 6
    c: Horizontal(g430)
    c: Coincident(g431,g430)
    c: PointOnObject(g431,g17)
    c: Coincident(g432,g430)
    c: PointOnObject(g432,g17)
    c: Coincident(g433,g431)
    c: Coincident(g433,g432)
    c: DistanceY(g430,g401) = 3.46
    c: Parallel(g375,g431)
    c: Parallel(g422,g432)
    c: DistanceX(g426,g430) = 18
    c: Distance(g434) = 6
    c: Horizontal(g434)
    c: Distance(g435) = 6
    c: Coincident(g435,g434)
    c: Distance(g436) = 6
    c: Coincident(g436,g435)
    c: DistanceY(g434,g412) = 1.73
    c: DistanceX(g398,g435) = 12
    c: Parallel(g417,g435)
    c: Parallel(g419,g436)
    c: Coincident(g437,g436)
    c: PointOnObject(g437,g18)
    c: Coincident(g438,g434)
    c: PointOnObject(g438,g18)
    c: Coincident(g439,g438)
    c: Coincident(g439,g437)
    c: Parallel(g420,g437)
    c: Parallel(g412,g438)
    c: Coincident(g441,g440)
    c: Parallel(g437,g440)
    c: Parallel(g421,g441)
    c: DistanceY(g440,g436) = 3.46
    c: DistanceX(g430,g440) = 18
    c: PointOnObject(g441,g19)
    c: PointOnObject(g440,g19)
    c: Distance(g442) = 6
    c: Horizontal(g442)
    c: Distance(g443) = 6
    c: Coincident(g443,g442)
    c: Distance(g444) = 6
    c: Coincident(g444,g443)
    c: Distance(g445) = 6
    c: Horizontal(g445)
    c: Coincident(g445,g444)
    c: Coincident(g446,g445)
    c: PointOnObject(g446,g14)
    c: Coincident(g447,g442)
    c: PointOnObject(g447,g14)
    c: Parallel(g389,g443)
    c: Parallel(g391,g444)
    c: Parallel(g417,g446)
    c: Parallel(g405,g447)
    c: DistanceY(g442,g408) = 3.46
    c: DistanceX(g356,g443) = 12
    c: Distance(g448) = 6
    c: Distance(g449) = 6
    c: Horizontal(g449)
    c: Coincident(g449,g448)
    c: Coincident(g450,g449)
    c: PointOnObject(g450,g14)
    c: DistanceY(g448,g46) = 3.46
    c: Parallel(g115,g448)
    c: Parallel(g110,g450)
    c: Distance(g451) = 6
    c: Angle(g-1,g451) = -1.0472
    c: Coincident(g451,g448)
    c: PointOnObject(g451,g14)
    c: DistanceX(g377,g448) = 12
    c: PointOnObject(g452,g18)
    c: Parallel(g438,g452)
    c: DistanceY(g438,g452) = 3.62
    c: Coincident(g453,g452)
    c: Coincident(g453,g14)
    c: PointOnObject(g452,g14)
    c: Distance(g454) = 6
    c: Angle(g-1,g454) = -1.0472
    c: PointOnObject(g455,g14)
    c: Coincident(g456,g454)
    c: PointOnObject(g456,g14)
    c: Horizontal(g456)
    c: DistanceX(g391,g454) = 12
    c: DistanceY(g434,g454) = 3.46
    c: Coincident(g455,g454)
    c: Coincident(g458,g457)
    c: Coincident(g458,g447)
    c: Coincident(g458,g446)
    c: Coincident(g460,g459)
    c: Coincident(g460,g452)
    c: Coincident(g460,g14)
    c: Coincident(g450,g457)
    c: Coincident(g451,g457)
    c: Coincident(g459,g455)
    c: Coincident(g456,g459)
    c: Coincident(g440,g461)
    c: Radius(g461) = 9.49
    c: Coincident(g461,g441)
    c: Parallel(g446,g455)
    c: Coincident(g462,g13)
    c: Coincident(g48,g462)
    c: Radius(g462) = 9.51
FEATURE [PartDesign::Pad] Pad
  Direction = (0,0,1)
  Length = 1
  Length2 = 10
  Profile = -> Sketch
  ReferenceAxis = -> Sketch [N_Axis]
  Refine = true
  Suppressed = false
  Type = 0
FEATURE [Sketcher::SketchObject] Sketch001
  ArcFitTolerance = 1e-06
  AttachmentSupport = -> [Pad]
  FullyConstrained = true
  MakeInternals = false
  MapMode = 5
  Placement = pos=(0,0,1) rot=(0,0,1;0rad)
  sketch-geometry (135):
    g0: Circle CenterX=12.35 CenterY=30.88 CenterZ=0 NormalX=0 NormalY=0 NormalZ=1 AngleXU=0 Radius=1.5
    g1: Circle CenterX=24 CenterY=24 CenterZ=0 NormalX=0 NormalY=0 NormalZ=1 AngleXU=0 Radius=1.5
    g2: Circle CenterX=20.35 CenterY=30.88 CenterZ=0 NormalX=0 NormalY=0 NormalZ=1 AngleXU=0 Radius=1.5
    g3: Circle CenterX=32 CenterY=24 CenterZ=0 NormalX=0 NormalY=0 NormalZ=1 AngleXU=0 Radius=1.5
    g4: Circle CenterX=8 CenterY=24 CenterZ=0 NormalX=0 NormalY=0 NormalZ=1 AngleXU=0 Radius=1.5
    g5: Circle CenterX=-1.9e-15 CenterY=24 CenterZ=0 NormalX=0 NormalY=0 NormalZ=1 AngleXU=0 Radius=1.5
    g6: Circle CenterX=-3.65 CenterY=30.88 CenterZ=0 NormalX=0 NormalY=0 NormalZ=1 AngleXU=0 Radius=1.5
    g7: Circle CenterX=8 CenterY=37.9 CenterZ=0 NormalX=0 NormalY=0 NormalZ=1 AngleXU=0 Radius=1.5
    g8: Circle CenterX=-6e-16 CenterY=37.9 CenterZ=0 NormalX=0 NormalY=0 NormalZ=1 AngleXU=0 Radius=1.5
    g9: Circle CenterX=24 CenterY=37.9 CenterZ=0 NormalX=0 NormalY=0 NormalZ=1 AngleXU=0 Radius=1.5
    g10: Circle CenterX=32 CenterY=37.9 CenterZ=0 NormalX=0 NormalY=0 NormalZ=1 AngleXU=0 Radius=1.5
    g11: Circle CenterX=36.35 CenterY=30.88 CenterZ=0 NormalX=0 NormalY=0 NormalZ=1 AngleXU=0 Radius=1.5
    g12: Circle CenterX=19.9 CenterY=16.98 CenterZ=0 NormalX=0 NormalY=0 NormalZ=1 AngleXU=0 Radius=1.5
    g13: Circle CenterX=11.9 CenterY=16.98 CenterZ=0 NormalX=0 NormalY=0 NormalZ=1 AngleXU=0 Radius=1.5
    g14: Circle CenterX=44.35 CenterY=30.88 CenterZ=0 NormalX=0 NormalY=0 NormalZ=1 AngleXU=0 Radius=1.5
    g15: Circle CenterX=48 CenterY=37.9 CenterZ=0 NormalX=0 NormalY=0 NormalZ=1 AngleXU=0 Radius=1.5
    g16: Circle CenterX=56 CenterY=37.9 CenterZ=0 NormalX=0 NormalY=0 NormalZ=1 AngleXU=0 Radius=1.5
    g17: Circle CenterX=48 CenterY=24 CenterZ=0 NormalX=0 NormalY=0 NormalZ=1 AngleXU=0 Radius=1.5
    g18: Circle CenterX=56 CenterY=24 CenterZ=0 NormalX=0 NormalY=0 NormalZ=1 AngleXU=0 Radius=1.5
    g19: Circle CenterX=35.9 CenterY=16.98 CenterZ=0 NormalX=0 NormalY=0 NormalZ=1 AngleXU=0 Radius=1.5
    g20: Circle CenterX=43.9 CenterY=16.98 CenterZ=0 NormalX=0 NormalY=0 NormalZ=1 AngleXU=0 Radius=1.5
    g21: Circle CenterX=48 CenterY=10.1 CenterZ=0 NormalX=0 NormalY=0 NormalZ=1 AngleXU=0 Radius=1.5
    g22: Circle CenterX=56 CenterY=10.1 CenterZ=0 NormalX=0 NormalY=0 NormalZ=1 AngleXU=0 Radius=1.5
    g23: Circle CenterX=59.9 CenterY=16.98 CenterZ=0 NormalX=0 NormalY=0 NormalZ=1 AngleXU=0 Radius=1.5
    g24: Circle CenterX=60.35 CenterY=30.88 CenterZ=0 NormalX=0 NormalY=0 NormalZ=1 AngleXU=0 Radius=1.5
    g25: Circle CenterX=68.35 CenterY=30.88 CenterZ=0 NormalX=0 NormalY=0 NormalZ=1 AngleXU=0 Radius=1.5
    g26: Circle CenterX=72 CenterY=37.9 CenterZ=0 NormalX=0 NormalY=0 NormalZ=1 AngleXU=0 Radius=1.5
    g27: Circle CenterX=72 CenterY=24 CenterZ=0 NormalX=0 NormalY=0 NormalZ=1 AngleXU=0 Radius=1.5
    g28: Circle CenterX=67.9 CenterY=16.98 CenterZ=0 NormalX=0 NormalY=0 NormalZ=1 AngleXU=0 Radius=1.5
    g29: Circle CenterX=72 CenterY=10.1 CenterZ=0 NormalX=0 NormalY=0 NormalZ=1 AngleXU=0 Radius=1.5
    g30: Circle CenterX=32 CenterY=10.1 CenterZ=0 NormalX=0 NormalY=0 NormalZ=1 AngleXU=0 Radius=1.5
    g31: Circle CenterX=24 CenterY=10.1 CenterZ=0 NormalX=0 NormalY=0 NormalZ=1 AngleXU=0 Radius=1.5
    g32: Circle CenterX=80 CenterY=37.9 CenterZ=0 NormalX=0 NormalY=0 NormalZ=1 AngleXU=0 Radius=1.5
    g33: Circle CenterX=84.35 CenterY=30.88 CenterZ=0 NormalX=0 NormalY=0 NormalZ=1 AngleXU=0 Radius=1.5
    g34: Circle CenterX=95.79 CenterY=37.13 CenterZ=0 NormalX=0 NormalY=0 NormalZ=1 AngleXU=0 Radius=1.5
    g35: Circle CenterX=104 CenterY=24 CenterZ=0 NormalX=0 NormalY=0 NormalZ=1 AngleXU=0 Radius=1.5
    g36: Circle CenterX=96 CenterY=24 CenterZ=0 NormalX=0 NormalY=0 NormalZ=1 AngleXU=0 Radius=1.5
    g37: Circle CenterX=80 CenterY=24 CenterZ=0 NormalX=0 NormalY=0 NormalZ=1 AngleXU=0 Radius=1.5
    g38: Circle CenterX=83.9 CenterY=16.98 CenterZ=0 NormalX=0 NormalY=0 NormalZ=1 AngleXU=0 Radius=1.5
    g39: Circle CenterX=91.9 CenterY=16.98 CenterZ=0 NormalX=0 NormalY=0 NormalZ=1 AngleXU=0 Radius=1.5
    g40: Circle CenterX=80 CenterY=10.1 CenterZ=0 NormalX=0 NormalY=0 NormalZ=1 AngleXU=0 Radius=1.5
    g41: Circle CenterX=83.9 CenterY=3.08 CenterZ=0 NormalX=0 NormalY=0 NormalZ=1 AngleXU=0 Radius=1.5
    g42: Circle CenterX=96 CenterY=10.1 CenterZ=0 NormalX=0 NormalY=0 NormalZ=1 AngleXU=0 Radius=1.5
    g43: Circle CenterX=91.9 CenterY=3.08 CenterZ=0 NormalX=0 NormalY=0 NormalZ=1 AngleXU=0 Radius=1.5
    g44: Circle CenterX=107.9 CenterY=16.98 CenterZ=0 NormalX=0 NormalY=0 NormalZ=1 AngleXU=0 Radius=1.5
    g45: Circle CenterX=96 CenterY=-3.8 CenterZ=0 NormalX=0 NormalY=0 NormalZ=1 AngleXU=0 Radius=1.5
    g46: Circle CenterX=104 CenterY=-17.7 CenterZ=0 NormalX=0 NormalY=0 NormalZ=1 AngleXU=0 Radius=1.5
    g47: Circle CenterX=96 CenterY=-17.7 CenterZ=0 NormalX=0 NormalY=0 NormalZ=1 AngleXU=0 Radius=1.5
    g48: Circle CenterX=91.9 CenterY=-10.82 CenterZ=0 NormalX=0 NormalY=0 NormalZ=1 AngleXU=0 Radius=1.5
    g49: Circle CenterX=83.9 CenterY=-10.82 CenterZ=0 NormalX=0 NormalY=0 NormalZ=1 AngleXU=0 Radius=1.5
    g50: Circle CenterX=80 CenterY=-3.8 CenterZ=0 NormalX=0 NormalY=0 NormalZ=1 AngleXU=0 Radius=1.5
    g51: Circle CenterX=72 CenterY=-3.8 CenterZ=0 NormalX=0 NormalY=0 NormalZ=1 AngleXU=0 Radius=1.5
    g52: Circle CenterX=67.9 CenterY=3.08 CenterZ=0 NormalX=0 NormalY=0 NormalZ=1 AngleXU=0 Radius=1.5
    g53: Circle CenterX=59.9 CenterY=3.08 CenterZ=0 NormalX=0 NormalY=0 NormalZ=1 AngleXU=0 Radius=1.5
    g54: Circle CenterX=56 CenterY=-3.8 CenterZ=0 NormalX=0 NormalY=0 NormalZ=1 AngleXU=0 Radius=1.5
    g55: Circle CenterX=48 CenterY=-3.8 CenterZ=0 NormalX=0 NormalY=0 NormalZ=1 AngleXU=0 Radius=1.5
    g56: Circle CenterX=43.9 CenterY=3.08 CenterZ=0 NormalX=0 NormalY=0 NormalZ=1 AngleXU=0 Radius=1.5
    g57: Circle CenterX=35.9 CenterY=3.08 CenterZ=0 NormalX=0 NormalY=0 NormalZ=1 AngleXU=0 Radius=1.5
    g58: Circle CenterX=19.9 CenterY=3.08 CenterZ=0 NormalX=0 NormalY=0 NormalZ=1 AngleXU=0 Radius=1.5
    g59: Circle CenterX=11.9 CenterY=3.08 CenterZ=0 NormalX=0 NormalY=0 NormalZ=1 AngleXU=0 Radius=1.5
    g60: Circle CenterX=8 CenterY=-3.8 CenterZ=0 NormalX=0 NormalY=0 NormalZ=1 AngleXU=0 Radius=1.5
    g61: Circle CenterX=11.9 CenterY=-10.82 CenterZ=0 NormalX=0 NormalY=0 NormalZ=1 AngleXU=0 Radius=1.5
    g62: Circle CenterX=19.9 CenterY=-10.82 CenterZ=0 NormalX=0 NormalY=0 NormalZ=1 AngleXU=0 Radius=1.5
    g63: Circle CenterX=24 CenterY=-3.8 CenterZ=0 NormalX=0 NormalY=0 NormalZ=1 AngleXU=0 Radius=1.5
    g64: Circle CenterX=32 CenterY=-3.8 CenterZ=0 NormalX=0 NormalY=0 NormalZ=1 AngleXU=0 Radius=1.5
    g65: Circle CenterX=35.9 CenterY=-10.82 CenterZ=0 NormalX=0 NormalY=0 NormalZ=1 AngleXU=0 Radius=1.5
    g66: Circle CenterX=43.9 CenterY=-10.82 CenterZ=0 NormalX=0 NormalY=0 NormalZ=1 AngleXU=0 Radius=1.5
    g67: Circle CenterX=59.9 CenterY=-10.82 CenterZ=0 NormalX=0 NormalY=0 NormalZ=1 AngleXU=0 Radius=1.5
    g68: Circle CenterX=67.9 CenterY=-10.82 CenterZ=0 NormalX=0 NormalY=0 NormalZ=1 AngleXU=0 Radius=1.5
    g69: Circle CenterX=72 CenterY=-17.7 CenterZ=0 NormalX=0 NormalY=0 NormalZ=1 AngleXU=0 Radius=1.5
    g70: Circle CenterX=80 CenterY=-17.7 CenterZ=0 NormalX=0 NormalY=0 NormalZ=1 AngleXU=0 Radius=1.5
    g71: Circle CenterX=56 CenterY=-17.7 CenterZ=0 NormalX=0 NormalY=0 NormalZ=1 AngleXU=0 Radius=1.5
    g72: Circle CenterX=48 CenterY=-17.7 CenterZ=0 NormalX=0 NormalY=0 NormalZ=1 AngleXU=0 Radius=1.5
    g73: Circle CenterX=32 CenterY=-17.7 CenterZ=0 NormalX=0 NormalY=0 NormalZ=1 AngleXU=0 Radius=1.5
    g74: Circle CenterX=24 CenterY=-17.7 CenterZ=0 NormalX=0 NormalY=0 NormalZ=1 AngleXU=0 Radius=1.5
    g75: Circle CenterX=8 CenterY=-17.7 CenterZ=0 NormalX=0 NormalY=0 NormalZ=1 AngleXU=0 Radius=1.5
    g76: Circle CenterX=11.9 CenterY=-24.72 CenterZ=0 NormalX=0 NormalY=0 NormalZ=1 AngleXU=0 Radius=1.5
    g77: Circle CenterX=19.9 CenterY=-24.72 CenterZ=0 NormalX=0 NormalY=0 NormalZ=1 AngleXU=0 Radius=1.5
    g78: Circle CenterX=35.9 CenterY=-24.72 CenterZ=0 NormalX=0 NormalY=0 NormalZ=1 AngleXU=0 Radius=1.5
    g79: Circle CenterX=43.9 CenterY=-24.72 CenterZ=0 NormalX=0 NormalY=0 NormalZ=1 AngleXU=0 Radius=1.5
    g80: Circle CenterX=59.9 CenterY=-24.72 CenterZ=0 NormalX=0 NormalY=0 NormalZ=1 AngleXU=0 Radius=1.5
    g81: Circle CenterX=67.9 CenterY=-24.72 CenterZ=0 NormalX=0 NormalY=0 NormalZ=1 AngleXU=0 Radius=1.5
    g82: Circle CenterX=83.9 CenterY=-24.72 CenterZ=0 NormalX=0 NormalY=0 NormalZ=1 AngleXU=0 Radius=1.5
    g83: Circle CenterX=91.9 CenterY=-24.72 CenterZ=0 NormalX=0 NormalY=0 NormalZ=1 AngleXU=0 Radius=1.5
    g84: Circle CenterX=96 CenterY=-31.6 CenterZ=0 NormalX=0 NormalY=0 NormalZ=1 AngleXU=0 Radius=1.5
    g85: Circle CenterX=102.6 CenterY=-31.6 CenterZ=0 NormalX=0 NormalY=0 NormalZ=1 AngleXU=0 Radius=1.5
    g86: Circle CenterX=80 CenterY=-31.6 CenterZ=0 NormalX=0 NormalY=0 NormalZ=1 AngleXU=0 Radius=1.5
    g87: Circle CenterX=72 CenterY=-31.6 CenterZ=0 NormalX=0 NormalY=0 NormalZ=1 AngleXU=0 Radius=1.5
    g88: Circle CenterX=68.18 CenterY=-37.99 CenterZ=0 NormalX=0 NormalY=0 NormalZ=1 AngleXU=0 Radius=1.5
    g89: Circle CenterX=59.25 CenterY=-37.99 CenterZ=0 NormalX=0 NormalY=0 NormalZ=1 AngleXU=0 Radius=1.5
    g90: Circle CenterX=56 CenterY=-31.6 CenterZ=0 NormalX=0 NormalY=0 NormalZ=1 AngleXU=0 Radius=1.5
    g91: Circle CenterX=48 CenterY=-31.6 CenterZ=0 NormalX=0 NormalY=0 NormalZ=1 AngleXU=0 Radius=1.5
    g92: Circle CenterX=44.24 CenterY=-37.99 CenterZ=0 NormalX=0 NormalY=0 NormalZ=1 AngleXU=0 Radius=1.5
    g93: Circle CenterX=35.52 CenterY=-37.99 CenterZ=0 NormalX=0 NormalY=0 NormalZ=1 AngleXU=0 Radius=1.5
    g94: Circle CenterX=32 CenterY=-31.6 CenterZ=0 NormalX=0 NormalY=0 NormalZ=1 AngleXU=0 Radius=1.5
    g95: Circle CenterX=24 CenterY=-31.6 CenterZ=0 NormalX=0 NormalY=0 NormalZ=1 AngleXU=0 Radius=1.5
    g96: Circle CenterX=20.44 CenterY=-37.99 CenterZ=0 NormalX=0 NormalY=0 NormalZ=1 AngleXU=0 Radius=1.5
    g97: Circle CenterX=8 CenterY=-31.6 CenterZ=0 NormalX=0 NormalY=0 NormalZ=1 AngleXU=0 Radius=1.5
    g98: Circle CenterX=11.56 CenterY=-37.99 CenterZ=0 NormalX=0 NormalY=0 NormalZ=1 AngleXU=0 Radius=1.5
    g99: Circle CenterX=-11.65 CenterY=30.88 CenterZ=0 NormalX=0 NormalY=0 NormalZ=1 AngleXU=0 Radius=1.5
    g100: Circle CenterX=-28.1 CenterY=16.98 CenterZ=0 NormalX=0 NormalY=0 NormalZ=1 AngleXU=0 Radius=1.5
    g101: Circle CenterX=-12.1 CenterY=16.98 CenterZ=0 NormalX=0 NormalY=0 NormalZ=1 AngleXU=0 Radius=1.5
    g102: Circle CenterX=-4.1 CenterY=16.98 CenterZ=0 NormalX=0 NormalY=0 NormalZ=1 AngleXU=0 Radius=1.5
    g103: Circle CenterX=1e-16 CenterY=10.1 CenterZ=0 NormalX=0 NormalY=0 NormalZ=1 AngleXU=0 Radius=1.5
    g104: Circle CenterX=8 CenterY=10.1 CenterZ=0 NormalX=0 NormalY=0 NormalZ=1 AngleXU=0 Radius=1.5
    g105: Circle CenterX=-4.1 CenterY=3.08 CenterZ=0 NormalX=0 NormalY=0 NormalZ=1 AngleXU=0 Radius=1.5
    g106: Circle CenterX=-12.1 CenterY=3.08 CenterZ=0 NormalX=0 NormalY=0 NormalZ=1 AngleXU=0 Radius=1.5
    g107: Circle CenterX=-28.1 CenterY=3.08 CenterZ=0 NormalX=0 NormalY=0 NormalZ=1 AngleXU=0 Radius=1.5
    g108: Circle CenterX=-36.1 CenterY=3.08 CenterZ=0 NormalX=0 NormalY=0 NormalZ=1 AngleXU=0 Radius=1.5
    g109: Circle CenterX=-28.1 CenterY=-10.82 CenterZ=0 NormalX=0 NormalY=0 NormalZ=1 AngleXU=0 Radius=1.5
    g110: Circle CenterX=-36.1 CenterY=-10.82 CenterZ=0 NormalX=0 NormalY=0 NormalZ=1 AngleXU=0 Radius=1.5
    g111: Circle CenterX=-24 CenterY=-4.03 CenterZ=0 NormalX=0 NormalY=0 NormalZ=1 AngleXU=0 Radius=1.5
    g112: Circle CenterX=-16 CenterY=-4.03 CenterZ=0 NormalX=0 NormalY=0 NormalZ=1 AngleXU=0 Radius=1.5
    g113: Circle CenterX=0 CenterY=-3.8 CenterZ=0 NormalX=0 NormalY=0 NormalZ=1 AngleXU=0 Radius=1.5
    g114: Circle CenterX=-4.1 CenterY=-10.82 CenterZ=0 NormalX=0 NormalY=0 NormalZ=1 AngleXU=0 Radius=1.5
    g115: Circle CenterX=-12.1 CenterY=-10.82 CenterZ=0 NormalX=0 NormalY=0 NormalZ=1 AngleXU=0 Radius=1.5
    g116: Circle CenterX=-16 CenterY=-17.88 CenterZ=0 NormalX=0 NormalY=0 NormalZ=1 AngleXU=0 Radius=1.5
    g117: Circle CenterX=-24 CenterY=-17.88 CenterZ=0 NormalX=0 NormalY=0 NormalZ=1 AngleXU=0 Radius=1.5
    g118: Circle CenterX=-28.1 CenterY=-24.72 CenterZ=0 NormalX=0 NormalY=0 NormalZ=1 AngleXU=0 Radius=1.5
    g119: Circle CenterX=-16 CenterY=-31.6 CenterZ=0 NormalX=0 NormalY=0 NormalZ=1 AngleXU=0 Radius=1.5
    g120: Circle CenterX=-12.1 CenterY=-24.72 CenterZ=0 NormalX=0 NormalY=0 NormalZ=1 AngleXU=0 Radius=1.5
    g121: Circle CenterX=-4.1 CenterY=-24.72 CenterZ=0 NormalX=0 NormalY=0 NormalZ=1 AngleXU=0 Radius=1.5
    g122: Circle CenterX=-1e-16 CenterY=-31.6 CenterZ=0 NormalX=0 NormalY=0 NormalZ=1 AngleXU=0 Radius=1.5
    g123: Circle CenterX=-3.5 CenterY=-37.99 CenterZ=0 NormalX=0 NormalY=0 NormalZ=1 AngleXU=0 Radius=1.5
    g124: Circle CenterX=-16 CenterY=23.66 CenterZ=0 NormalX=0 NormalY=0 NormalZ=1 AngleXU=0 Radius=1.5
    g125: Circle CenterX=-24 CenterY=23.66 CenterZ=0 NormalX=0 NormalY=0 NormalZ=1 AngleXU=0 Radius=1.5
    g126: Circle CenterX=-16 CenterY=9.81 CenterZ=0 NormalX=0 NormalY=0 NormalZ=1 AngleXU=0 Radius=1.5
    g127: Circle CenterX=-24 CenterY=9.81 CenterZ=0 NormalX=0 NormalY=0 NormalZ=1 AngleXU=0 Radius=1.5
    g128: Circle CenterX=-5e-16 CenterY=-17.7 CenterZ=0 NormalX=0 NormalY=0 NormalZ=1 AngleXU=0 Radius=1.5
    g129: Circle CenterX=92.35 CenterY=30.88 CenterZ=0 NormalX=0 NormalY=0 NormalZ=1 AngleXU=0 Radius=1.5
    g130: Circle CenterX=92.35 CenterY=-37.99 CenterZ=0 NormalX=0 NormalY=0 NormalZ=1 AngleXU=0 Radius=1.5
    g131: Circle CenterX=83.37 CenterY=-37.99 CenterZ=0 NormalX=0 NormalY=0 NormalZ=1 AngleXU=0 Radius=1.5
    g132: Circle CenterX=-26.03 CenterY=27.49 CenterZ=0 NormalX=0 NormalY=0 NormalZ=1 AngleXU=0 Radius=1.5
    g133: Circle CenterX=-14.36 CenterY=35.21 CenterZ=0 NormalX=0 NormalY=0 NormalZ=1 AngleXU=0 Radius=1.5
    g134: Circle CenterX=-33.81 CenterY=16.98 CenterZ=0 NormalX=0 NormalY=0 NormalZ=1 AngleXU=0 Radius=1.5
  constraints (405):
    c: Radius(g0) = 1.5
    c: Radius(g1) = 1.5
    c: Radius(g2) = 1.5
    c: Equal(g1,g3)
    c: Horizontal(g1,g3)
    c: Equal(g0,g7)
    c: Equal(g7,g8)
    c: Equal(g8,g6)
    c: Equal(g6,g5)
    c: Equal(g5,g4)
    c: Equal(g0,g13)
    c: Equal(g13,g12)
    c: Equal(g12,g11)
    c: Equal(g11,g10)
    c: Equal(g10,g9)
    c: DistanceX(g0,g2) = 8
    c: DistanceX(g8,g7) = 8
    c: DistanceX(g5,g4) = 8
    c: DistanceX(g9,g10) = 8
    c: DistanceX(g1,g3) = 8
    c: DistanceX(g13,g12) = 8
    c: Horizontal(g8,g7)
    c: Horizontal(g7,g9)
    c: Horizontal(g9,g10)
    c: Horizontal(g6,g0)
    c: Horizontal(g0,g2)
    c: Horizontal(g2,g11)
    c: Horizontal(g5,g4)
    c: Horizontal(g4,g1)
    c: DistanceX(g6,g0) = 16
    c: DistanceX(g4,g1) = 16
    c: Equal(g11,g14)
    c: Equal(g14,g20)
    c: Equal(g20,g19)
    c: Equal(g19,g30)
    c: Equal(g30,g21)
    c: Equal(g21,g56)
    c: Equal(g56,g57)
    c: Equal(g57,g31)
    c: Equal(g31,g17)
    c: Equal(g17,g18)
    c: Equal(g18,g23)
    c: Equal(g23,g22)
    c: Equal(g22,g53)
    c: Equal(g53,g24)
    c: Equal(g24,g16)
    c: Equal(g16,g15)
    c: Equal(g15,g25)
    c: Equal(g25,g26)
    c: Equal(g26,g32)
    c: Equal(g32,g33)
    c: Equal(g33,g37)
    c: Equal(g37,g27)
    c: Equal(g27,g28)
    c: Equal(g28,g29)
    c: Equal(g29,g40)
    c: Equal(g40,g38)
    c: Equal(g38,g39)
    c: Equal(g39,g36)
    c: Equal(g34,g35)
    c: Equal(g35,g44)
    c: Equal(g44,g42)
    c: Equal(g40,g41)
    c: Equal(g41,g43)
    c: Equal(g43,g52)
    c: Equal(g52,g54)
    c: Equal(g54,g51)
    c: Equal(g51,g50)
    c: Equal(g50,g45)
    c: Equal(g45,g48)
    c: Equal(g48,g49)
    c: Equal(g49,g70)
    c: Equal(g70,g69)
    c: Equal(g69,g68)
    c: Equal(g68,g67)
    c: Equal(g67,g71)
    c: Equal(g71,g46)
    c: Equal(g46,g47)
    c: Equal(g83,g84)
    c: Equal(g84,g85)
    c: Equal(g86,g82)
    c: Equal(g82,g87)
    c: Equal(g87,g81)
    c: Equal(g81,g80)
    c: Equal(g80,g90)
    c: Equal(g90,g89)
    c: Equal(g89,g88)
    c: Equal(g54,g55)
    c: Equal(g55,g72)
    c: Equal(g72,g66)
    c: Equal(g66,g64)
    c: Equal(g64,g65)
    c: Equal(g65,g73)
    c: Equal(g73,g78)
    c: Equal(g78,g79)
    c: Equal(g79,g91)
    c: Equal(g91,g92)
    c: Equal(g92,g93)
    c: Equal(g93,g94)
    c: Equal(g94,g95)
    c: Equal(g95,g96)
    c: Equal(g96,g98)
    c: Equal(g98,g97)
    c: Equal(g97,g76)
    c: Equal(g76,g77)
    c: Equal(g77,g74)
    c: Equal(g74,g62)
    c: Equal(g62,g63)
    c: Equal(g63,g61)
    c: Equal(g61,g75)
    c: Equal(g75,g60)
    c: Equal(g60,g59)
    c: Equal(g59,g58)
    c: Equal(g60,g113)
    c: Equal(g113,g114)
    c: Equal(g121,g122)
    c: Equal(g122,g123)
    c: Equal(g123,g119)
    c: Equal(g119,g120)
    c: Equal(g120,g116)
    c: Equal(g116,g118)
    c: Equal(g118,g117)
    c: Equal(g117,g109)
    c: Equal(g109,g110)
    c: Equal(g110,g111)
    c: Equal(g111,g112)
    c: Equal(g112,g106)
    c: Equal(g106,g105)
    c: Equal(g105,g107)
    c: Equal(g107,g108)
    c: Equal(g100,g103)
    c: Equal(g103,g104)
    c: Equal(g101,g102)
    c: DistanceX(g25,g33) = 16
    c: Horizontal(g25,g24)
    c: Horizontal(g24,g14)
    c: Horizontal(g14,g11)
    c: DistanceX(g24,g25) = 8
    c: DistanceX(g14,g24) = 16
    c: DistanceX(g11,g14) = 8
    c: DistanceX(g2,g11) = 16
    c: Horizontal(g6,g99)
    c: DistanceX(g99,g6) = 8
    c: Horizontal(g36,g35)
    c: DistanceX(g36,g35) = 8
    c: Horizontal(g36,g37)
    c: Horizontal(g37,g27)
    c: Horizontal(g27,g18)
    c: Horizontal(g18,g17)
    c: Horizontal(g17,g3)
    c: DistanceX(g37,g36) = 16
    c: DistanceX(g27,g37) = 8
    c: DistanceX(g18,g27) = 16
    c: DistanceX(g17,g18) = 8
    c: DistanceX(g3,g17) = 16
    c: DistanceX(g26,g32) = 8
    c: Horizontal(g32,g26)
    c: Horizontal(g26,g16)
    c: Horizontal(g16,g15)
    c: DistanceX(g15,g16) = 8
    c: DistanceX(g16,g26) = 16
    c: Horizontal(g15,g10)
    c: DistanceX(g10,g15) = 16
    c: DistanceX(g7,g9) = 16
    c: Equal(g5,g124)
    c: DistanceX(g124,g5) = 16
    c: Equal(g124,g125)
    c: Horizontal(g124,g125)
    c: DistanceX(g125,g124) = 8
    c: Horizontal(g39,g44)
    c: Horizontal(g39,g38)
    c: Horizontal(g38,g28)
    c: Horizontal(g28,g23)
    c: Horizontal(g23,g20)
    c: Horizontal(g20,g19)
    c: Horizontal(g19,g12)
    c: Horizontal(g12,g13)
    c: Horizontal(g13,g102)
    c: Horizontal(g102,g101)
    c: Horizontal(g101,g100)
    c: DistanceX(g38,g39) = 8
    c: DistanceX(g28,g38) = 16
    c: DistanceX(g39,g44) = 16
    c: DistanceX(g23,g28) = 8
    c: DistanceX(g20,g23) = 16
    c: DistanceX(g19,g20) = 8
    c: DistanceX(g12,g19) = 16
    c: DistanceX(g102,g13) = 16
    c: DistanceX(g101,g102) = 8
    c: DistanceX(g100,g101) = 16
    c: Horizontal(g40,g42)
    c: Horizontal(g40,g29)
    c: Horizontal(g29,g22)
    c: Horizontal(g22,g21)
    c: Horizontal(g21,g30)
    c: Horizontal(g30,g31)
    c: Horizontal(g31,g104)
    c: Horizontal(g104,g103)
    c: DistanceX(g29,g40) = 8
    c: DistanceX(g40,g42) = 16
    c: DistanceX(g22,g29) = 16
    c: DistanceX(g21,g22) = 8
    c: DistanceX(g30,g21) = 16
    c: DistanceX(g31,g30) = 8
    c: DistanceX(g104,g31) = 16
    c: DistanceX(g103,g104) = 8
    c: Equal(g106,g126)
    c: Equal(g126,g127)
    c: DistanceX(g126,g103) = 16
    c: Horizontal(g126,g127)
    c: DistanceX(g127,g126) = 8
    c: Horizontal(g41,g43)
    c: DistanceX(g41,g43) = 8
    c: Horizontal(g41,g52)
    c: Horizontal(g52,g53)
    c: Horizontal(g53,g56)
    c: Horizontal(g56,g57)
    c: Horizontal(g57,g58)
    c: Horizontal(g58,g59)
    c: Horizontal(g59,g105)
    c: Horizontal(g105,g106)
    c: Horizontal(g106,g107)
    c: Horizontal(g107,g108)
    c: DistanceX(g52,g41) = 16
    c: DistanceX(g53,g52) = 8
    c: DistanceX(g56,g53) = 16
    c: DistanceX(g57,g56) = 8
    c: DistanceX(g58,g57) = 16
    c: DistanceX(g59,g58) = 8
    c: DistanceX(g105,g59) = 16
    c: DistanceX(g106,g105) = 8
    c: DistanceX(g107,g106) = 16
    c: DistanceX(g108,g107) = 8
    c: Horizontal(g50,g45)
    c: DistanceX(g50,g45) = 16
    c: Horizontal(g50,g51)
    c: Horizontal(g51,g54)
    c: Horizontal(g54,g55)
    c: Horizontal(g55,g64)
    c: Horizontal(g64,g63)
    c: Horizontal(g63,g60)
    c: Horizontal(g60,g113)
    c: Horizontal(g112,g111)
    c: DistanceX(g51,g50) = 8
    c: DistanceX(g54,g51) = 16
    c: DistanceX(g55,g54) = 8
    c: DistanceX(g64,g55) = 16
    c: DistanceX(g63,g64) = 8
    c: DistanceX(g60,g63) = 16
    c: DistanceX(g113,g60) = 8
    c: DistanceX(g112,g113) = 16
    c: DistanceX(g111,g112) = 8
    c: Horizontal(g48,g49)
    c: Horizontal(g49,g68)
    c: Horizontal(g68,g67)
    c: Horizontal(g67,g66)
    c: Horizontal(g66,g65)
    c: Horizontal(g65,g62)
    c: Horizontal(g62,g61)
    c: Horizontal(g61,g114)
    c: Horizontal(g114,g115)
    c: Horizontal(g115,g109)
    c: Horizontal(g109,g110)
    c: DistanceX(g49,g48) = 8
    c: DistanceX(g68,g49) = 16
    c: DistanceX(g67,g68) = 8
    c: DistanceX(g66,g67) = 16
    c: DistanceX(g65,g66) = 8
    c: DistanceX(g62,g65) = 16
    c: DistanceX(g61,g62) = 8
    c: DistanceX(g114,g61) = 16
    c: DistanceX(g115,g114) = 8
    c: DistanceX(g109,g115) = 16
    c: DistanceX(g110,g109) = 8
    c: Horizontal(g47,g46)
    c: DistanceX(g47,g46) = 8
    c: Horizontal(g47,g70)
    c: Horizontal(g70,g69)
    c: Horizontal(g69,g71)
    c: Horizontal(g71,g72)
    c: Horizontal(g72,g73)
    c: Horizontal(g73,g74)
    c: Horizontal(g74,g75)
    c: Horizontal(g116,g117)
    c: DistanceX(g70,g47) = 16
    c: DistanceX(g69,g70) = 8
    c: DistanceX(g71,g69) = 16
    c: DistanceX(g72,g71) = 8
    c: DistanceX(g73,g72) = 16
    c: DistanceX(g74,g73) = 8
    c: DistanceX(g75,g74) = 16
    c: DistanceX(g117,g116) = 8
    c: Equal(g75,g128)
    c: Horizontal(g75,g128)
    c: DistanceX(g128,g75) = 8
    c: DistanceX(g116,g128) = 16
    c: Horizontal(g83,g82)
    c: Horizontal(g82,g81)
    c: Horizontal(g81,g80)
    c: Horizontal(g80,g79)
    c: Horizontal(g78,g77)
    c: Horizontal(g77,g76)
    c: Horizontal(g76,g121)
    c: Horizontal(g121,g120)
    c: Horizontal(g120,g118)
    c: DistanceX(g118,g120) = 16
    c: DistanceX(g120,g121) = 8
    c: DistanceX(g121,g76) = 16
    c: DistanceX(g76,g77) = 8
    c: DistanceX(g77,g78) = 16
    c: DistanceX(g78,g79) = 8
    c: DistanceX(g79,g80) = 16
    c: DistanceX(g80,g81) = 8
    c: DistanceX(g81,g82) = 16
    c: DistanceX(g82,g83) = 8
    c: Horizontal(g84,g85)
    c: DistanceX(g84,g85) = 6.6
    c: Horizontal(g84,g86)
    c: Horizontal(g86,g87)
    c: Horizontal(g87,g90)
    c: Horizontal(g90,g91)
    c: Horizontal(g91,g94)
    c: Horizontal(g94,g95)
    c: Horizontal(g95,g97)
    c: Horizontal(g97,g122)
    c: Horizontal(g122,g119)
    c: DistanceX(g119,g122) = 16
    c: DistanceX(g122,g97) = 8
    c: DistanceX(g97,g95) = 16
    c: DistanceX(g95,g94) = 8
    c: DistanceX(g94,g91) = 16
    c: DistanceX(g91,g90) = 8
    c: DistanceX(g90,g87) = 16
    c: DistanceX(g87,g86) = 8
    c: DistanceX(g86,g84) = 16
    c: Vertical(g39,g43)
    c: Vertical(g43,g48)
    c: Vertical(g48,g83)
    c: DistanceY(g43,g39) = 13.9
    c: DistanceY(g48,g43) = 13.9
    c: DistanceY(g83,g48) = 13.9
    c: DistanceX(g113,g-1) = 0
    c: Vertical(g50,g40)
    c: Vertical(g40,g37)
    c: Vertical(g37,g32)
    c: Vertical(g50,g70)
    c: Vertical(g70,g86)
    c: DistanceX(g105,g-1) = 4.1
    c: Horizontal(g33,g25)
    c: Equal(g33,g129)
    c: Horizontal(g33,g129)
    c: DistanceX(g33,g129) = 8
    c: DistanceY(g39,g129) = 13.9
    c: DistanceY(g113,g-1) = 3.8
    c: DistanceY(g40,g37) = 13.9
    c: DistanceY(g50,g40) = 13.9
    c: DistanceY(g70,g50) = 13.9
    c: DistanceY(g86,g70) = 13.9
    c: DistanceY(g116,g128) = 0.18
    c: DistanceY(g112,g113) = 0.23
    c: DistanceY(g126,g103) = 0.29
    c: DistanceY(g124,g5) = 0.34
    c: DistanceY(g5,g8) = 13.9
    c: DistanceY(g-1,g105) = 3.08
    c: DistanceX(g6,g-1) = 3.65
    c: Equal(g130,g131)
    c: Horizontal(g130,g131)
    c: Horizontal(g131,g88)
    c: Horizontal(g88,g89)
    c: DistanceY(g130,g83) = 13.27
    c: DistanceX(g130,g84) = 3.65
    c: DistanceX(g131,g130) = 8.98
    c: DistanceX(g88,g131) = 15.19
    c: DistanceX(g89,g88) = 8.93
    c: Horizontal(g89,g92)
    c: DistanceX(g92,g89) = 15.01
    c: Horizontal(g92,g93)
    c: DistanceX(g93,g92) = 8.72
    c: Horizontal(g93,g96)
    c: DistanceX(g96,g93) = 15.08
    c: Horizontal(g96,g98)
    c: DistanceX(g98,g96) = 8.88
    c: Horizontal(g98,g123)
    c: DistanceX(g123,g98) = 15.06
    c: Equal(g39,g42)
    c: Equal(g46,g85)
    c: Equal(g84,g130)
    c: Equal(g83,g82)
    c: Horizontal(g79,g78)
    c: Equal(g97,g122)
    c: Equal(g114,g115)
    c: Equal(g59,g104)
    c: Equal(g126,g101)
    c: Equal(g124,g99)
    c: DistanceX(g32,g34) = 15.79
    c: DistanceY(g129,g34) = 6.25
    c: Equal(g125,g132)
    c: DistanceY(g125,g132) = 3.83
    c: DistanceX(g132,g125) = 2.03
    c: Equal(g99,g133)
    c: DistanceY(g99,g133) = 4.33
    c: DistanceX(g133,g99) = 2.71
    c: Equal(g100,g134)
    c: Horizontal(g100,g134)
    c: DistanceX(g134,g100) = 5.71
FEATURE [PartDesign::Pad] Pad001
  BaseFeature = -> Pad
  Direction = (0,0,1)
  Length = 3
  Length2 = 3
  Profile = -> Sketch001
  ReferenceAxis = -> Sketch001 [N_Axis]
  Refine = true
  Suppressed = false
  Type = 4
FEATURE [PartDesign::Fillet] Fillet
  Base = -> Pad001 [Edge1912,Edge1886,Edge1888,Edge1910,Face894,Edge1920,Edge1916,Edge1890,Edge1878,Edge1884,Edge1876,Edge1880,Face874,Edge1772,Edge1782,Edge1774,Edge1770,Edge1746,Edge1744,Face811,Edge1776,Edge1778,Edge1784,Edge1932,Face904,Edge1918,Face902,Edge1924,Edge1922,Face883,Face888,Face887,Face886,Face878,Face884,Face837,Edge1798,Face827,Edge1790,Edge1788,+95 more]
  BaseFeature = -> Pad001
  Radius = 1.4
  Refine = true
  SupportTransform = false
  Suppressed = false
  UseAllEdges = false
FEATURE [PartDesign::Fillet] Fillet001
  Base = -> Fillet [Face944,Edge2015,Edge2039,Face958,Face959,Face963,Edge2145,Edge2143,Edge2155,Face1027,Face1028,Face1016,Face1011,Face946,Edge2045,Face961,Edge2053,Edge2149,Face1014,Edge2159,Edge2183,Edge2185,Edge2189,Edge2201,Edge2187,Edge2191,Edge2161,Edge2167,Face1013,Edge2067,Edge2049,Edge2055,Edge2019,Edge2023,Edge2011,Edge2021,Edge2025,Edge2035,Edge2057,Edge2059,+95 more]
  BaseFeature = -> Fillet
  Radius = 0.99
  Refine = true
  SupportTransform = false
  Suppressed = false
  UseAllEdges = false
FEATURE [PartDesign::Body] Body
  AllowCompound = false
  Group = -> [Sketch,Pad,Sketch001,Pad001,Fillet,Fillet001]
  Origin = -> Origin
  Tip = -> Fillet001
